FCSTD DOCUMENT  (FreeCAD 1.0R38641 +468 (Git))
Label: cad_assembly
License: All rights reserved
LicenseURL: https://en.wikipedia.org/wiki/All_rights_reserved
objects: App::Link×18, App::FeaturePython×17, Assembly::JointGroup×1, Assembly::AssemblyObject×1
EXTERNAL_REF file=cad_frame_top.FCStd obj=Body
EXTERNAL_REF file=k1_motor_mount_left.FCStd obj=Part
EXTERNAL_REF file=k1_motor_mount_right.FCStd obj=Part
EXTERNAL_REF file=k1_front_idler_left.FCStd obj=Part
EXTERNAL_REF file=k1_front_idler_right.FCStd obj=Part
EXTERNAL_REF file=k1_joint_left.FCStd obj=Part
EXTERNAL_REF file=cad_rail_mgn12_x.FCStd obj=Body
EXTERNAL_REF file=k1_joint_right.FCStd obj=Part
EXTERNAL_REF file=k1_rail_mount.FCStd obj=Part
EXTERNAL_REF file=k1_tensioner_left.FCStd obj=Part
EXTERNAL_REF file=k1_tensioner_right.FCStd obj=Part
EXTERNAL_REF file=cad_20x10x2.FCStd obj=Body
EXTERNAL_REF file=k1_toolhead_20x10.FCStd obj=Part
EXTERNAL_REF file=cad_rail_mgn12_y.FCStd obj=Body
EXTERNAL_REF file=k1_motor_mount_couplers_stock_left.FCStd obj=Part
EXTERNAL_REF file=k1_motor_mount_couplers_stock_right.FCStd obj=Part

FEATURE [App::Link] cad_frame_top
  LinkPlacement = pos=(0,0,0) rot=(-0.926776,-0.056516,-0.371338;0rad)
  LinkedObject = -> <external cad_frame_top.FCStd>#Body
  Placement = pos=(0,0,0) rot=(-0.926776,-0.056516,-0.371338;0rad)
FEATURE [App::FeaturePython] GroundedJoint  # Assembly grounded joint (typed FeaturePython)
  ObjectToGround = -> cad_frame_top
  Placement = pos=(0,0,0) rot=(-0.927137,-0.056538,-0.371482;0rad)
FEATURE [App::Link] k1_motor_mount_left_part
  LinkPlacement = pos=(-212.641,150.472,-35.0551) rot=(-0.926776,-0.056516,-0.371338;0rad)
  LinkedObject = -> <external k1_motor_mount_left.FCStd>#Part
  Placement = pos=(-212.641,150.472,-35.0551) rot=(-0.926776,-0.056516,-0.371338;0rad)
FEATURE [App::FeaturePython] Joint  label="frame_motor_left"  # Assembly joint (typed FeaturePython)
  Activated = true
  AngleMax = 0
  AngleMin = 0
  Detach1 = false
  Detach2 = false
  Distance = 0
  Distance2 = 0
  EnableAngleMax = false
  EnableAngleMin = false
  EnableLengthMax = false
  EnableLengthMin = false
  JointType = 0 (Fixed)
  LengthMax = 0
  LengthMin = 0
  Offset2 = pos=(0,0,0) rot=(0,0,1;1.5708rad)
  Placement1 = pos=(52.6406,991.528,40.055) rot=(-0.707107,0,0.707107;3.14159rad)
  Placement2 = pos=(-212,192,5) rot=(0,-1.00039,0;4.71239rad)
  Reference1 = -> Assembly [k1_motor_mount_left_part.Body.Edge272,k1_motor_mount_left_part.Body.Edge272]
  Reference2 = -> Assembly [cad_frame_top.Edge152,cad_frame_top.Edge152]
FEATURE [App::Link] k1_motor_mount_right_part
  LinkPlacement = pos=(135.359,150.472,-35.055) rot=(-0.926776,-0.056516,-0.371338;0rad)
  LinkedObject = -> <external k1_motor_mount_right.FCStd>#Part
  Placement = pos=(135.359,150.472,-35.055) rot=(-0.926776,-0.056516,-0.371338;0rad)
FEATURE [App::FeaturePython] Joint001  label="frame_motor_right"  # Assembly joint (typed FeaturePython)
  Activated = true
  AngleMax = 0
  AngleMin = 0
  Detach1 = false
  Detach2 = false
  Distance = 0
  Distance2 = 0
  EnableAngleMax = false
  EnableAngleMin = false
  EnableLengthMax = false
  EnableLengthMin = false
  JointType = 0 (Fixed)
  LengthMax = 0
  LengthMin = 0
  Offset2 = pos=(0,0,0) rot=(0,0,-1;1.5708rad)
  Placement1 = pos=(305.641,991.528,40.055) rot=(0,-1,0;1.5708rad)
  Placement2 = pos=(212,192,5) rot=(0.707382,0,0.707382;3.14159rad)
  Reference1 = -> Assembly [k1_motor_mount_right_part.Body.Edge6,k1_motor_mount_right_part.Body.Edge6]
  Reference2 = -> Assembly [cad_frame_top.Edge216,cad_frame_top.Edge216]
FEATURE [App::Link] k1_front_idler_left_part
  LinkPlacement = pos=(-212,-211.265,-35.0549) rot=(-0.926776,-0.056516,-0.371338;0rad)
  LinkedObject = -> <external k1_front_idler_left.FCStd>#Part
  Placement = pos=(-212,-211.265,-35.0549) rot=(-0.926776,-0.056516,-0.371338;0rad)
FEATURE [App::Link] k1_front_idler_right_part
  LinkPlacement = pos=(212,-211.265,-35.0549) rot=(-0.926776,-0.056516,-0.371338;0rad)
  LinkedObject = -> <external k1_front_idler_right.FCStd>#Part
  Placement = pos=(212,-211.265,-35.0549) rot=(-0.926776,-0.056516,-0.371338;0rad)
FEATURE [App::Link] k1_joint_left_part
  LinkPlacement = pos=(-182.615,35.6211,-29.1099) rot=(0.57735,-0.57735,0.57735;2.0944rad)
  LinkedObject = -> <external k1_joint_left.FCStd>#Part
  Placement = pos=(-182.615,35.6211,-29.1099) rot=(0.57735,-0.57735,0.57735;2.0944rad)
FEATURE [App::FeaturePython] Joint007  label="frame_front_idler_right"  # Assembly joint (typed FeaturePython)
  Activated = true
  AngleMax = 0
  AngleMin = 0
  Detach1 = false
  Detach2 = false
  Distance = 0
  Distance2 = 0
  EnableAngleMax = false
  EnableAngleMin = false
  EnableLengthMax = false
  EnableLengthMin = false
  JointType = 0 (Fixed)
  LengthMax = 0
  LengthMin = 0
  Placement1 = pos=(212,-192,5) rot=(0.577575,0.577575,0.577575;2.0944rad)
  Placement2 = pos=(0,19.265,40.055) rot=(0.57735,0.57735,0.57735;2.0944rad)
  Reference1 = -> Assembly [cad_frame_top.Edge217,cad_frame_top.Edge217]
  Reference2 = -> Assembly [k1_front_idler_right_part.Body.Edge47,k1_front_idler_right_part.Body.Edge47]
FEATURE [App::Link] cad_rail_mgn12_x
  LinkPlacement = pos=(191.885,27.491,-25.2799) rot=(0.57735,0.57735,-0.57735;4.18879rad)
  LinkedObject = -> <external cad_rail_mgn12_x.FCStd>#Body
  Placement = pos=(191.885,27.491,-25.2799) rot=(0.57735,0.57735,-0.57735;4.18879rad)
FEATURE [App::Link] k1_joint_right_part
  LinkPlacement = pos=(182.385,35.621,-29.1099) rot=(0.57735,-0.57735,0.57735;2.0944rad)
  LinkedObject = -> <external k1_joint_right.FCStd>#Part
  Placement = pos=(182.385,35.621,-29.1099) rot=(0.57735,-0.57735,0.57735;2.0944rad)
FEATURE [App::FeaturePython] Joint011  label="frame_front_idler_left"  # Assembly joint (typed FeaturePython)
  Activated = true
  AngleMax = 0
  AngleMin = 0
  Detach1 = false
  Detach2 = false
  Distance = 0
  Distance2 = 0
  EnableAngleMax = false
  EnableAngleMin = false
  EnableLengthMax = false
  EnableLengthMin = false
  JointType = 0 (Fixed)
  LengthMax = 0
  LengthMin = 0
  Offset2 = pos=(0,0,0) rot=(0,0,1;3.14159rad)
  Placement1 = pos=(-212,-192,5) rot=(0.577575,0.577575,0.577575;2.0944rad)
  Placement2 = pos=(0,19.265,40.055) rot=(0.57735,0.57735,-0.57735;4.18879rad)
  Reference1 = -> Assembly [cad_frame_top.Edge153,cad_frame_top.Edge153]
  Reference2 = -> Assembly [k1_front_idler_left_part.Body.Edge12,k1_front_idler_left_part.Body.Edge12]
FEATURE [App::Link] k1_rail_mount_part  label="k1_rail_mount_left"
  LinkPlacement = pos=(187.115,-20.5,12.89) rot=(-0.926775,-0.056516,-0.371338;0rad)
  LinkedObject = -> <external k1_rail_mount.FCStd>#Part
  Placement = pos=(187.115,-20.5,12.89) rot=(-0.926775,-0.056516,-0.371338;0rad)
FEATURE [App::Link] k1_rail_mount_part001  label="k1_rail_mount_right"
  LinkPlacement = pos=(-187.115,19.5,12.89) rot=(0,0,1;3.14159rad)
  LinkedObject = -> <external k1_rail_mount.FCStd>#Part
  Placement = pos=(-187.115,19.5,12.89) rot=(0,0,1;3.14159rad)
FEATURE [App::Link] k1_tensioner_left_part
  LinkPlacement = pos=(-174.295,195.1,4.54494) rot=(0.57735,0.57735,0.57735;2.0944rad)
  LinkedObject = -> <external k1_tensioner_left.FCStd>#Part
  Placement = pos=(-174.295,195.1,4.54494) rot=(0.57735,0.57735,0.57735;2.0944rad)
FEATURE [App::FeaturePython] Joint014  label="motor_left_tensioner"  # Assembly joint (typed FeaturePython)
  Activated = true
  AngleMax = 0
  AngleMin = 0
  Detach1 = false
  Detach2 = false
  Distance = 0
  Distance2 = 0
  EnableAngleMax = false
  EnableAngleMin = false
  EnableLengthMax = false
  EnableLengthMin = false
  JointType = 3 (Slider)
  LengthMax = 0
  LengthMin = 0
  Offset2 = pos=(0,0,0) rot=(0,0,1;1.5708rad)
  Placement1 = pos=(7,-27.15,2) rot=(0,0,1;0rad)
  Placement2 = pos=(86.3406,1001.63,12.45) rot=(-0.57735,-0.57735,0.57735;2.0944rad)
  Reference1 = -> Assembly [k1_tensioner_left_part.Body.Edge23,k1_tensioner_left_part.Body.Edge23]
  Reference2 = -> Assembly [k1_motor_mount_left_part.Body.Edge192,k1_motor_mount_left_part.Body.Edge192]
FEATURE [App::Link] k1_tensioner_right_part
  LinkPlacement = pos=(175.227,205.85,2.49494) rot=(-0.57735,0.57735,0.57735;4.18879rad)
  LinkedObject = -> <external k1_tensioner_right.FCStd>#Part
  Placement = pos=(175.227,205.85,2.49494) rot=(-0.57735,0.57735,0.57735;4.18879rad)
FEATURE [App::FeaturePython] Joint015  label="motor_right_tensioner"  # Assembly joint (typed FeaturePython)
  Activated = true
  AngleMax = 0
  AngleMin = 0
  Detach1 = false
  Detach2 = false
  Distance = 0
  Distance2 = 0
  EnableAngleMax = false
  EnableAngleMin = false
  EnableLengthMax = false
  EnableLengthMin = false
  JointType = 3 (Slider)
  LengthMax = 0
  LengthMin = 0
  Offset2 = pos=(0,0,0) rot=(0,0,1;1.5708rad)
  Placement1 = pos=(3.75,-9,2) rot=(0,0,1;0rad)
  Placement2 = pos=(271.941,1001.63,28.55) rot=(-0.57735,0.57735,0.57735;4.18879rad)
  Reference1 = -> Assembly [k1_tensioner_right_part.Body.Edge78,k1_tensioner_right_part.Body.Edge78]
  Reference2 = -> Assembly [k1_motor_mount_right_part.Body.Edge283,k1_motor_mount_right_part.Body.Edge283]
FEATURE [App::Link] cad_20x10x2
  LinkPlacement = pos=(204.385,31.491,-34.2799) rot=(0.707107,0.707107,0;3.14159rad)
  LinkedObject = -> <external cad_20x10x2.FCStd>#Body
  Placement = pos=(204.385,31.491,-34.2799) rot=(0.707107,0.707107,0;3.14159rad)
FEATURE [App::Link] k1_toolhead_20x10_part
  LinkPlacement = pos=(-33.1127,27.001,-47.3799) rot=(0,0,1;4.71239rad)
  LinkedObject = -> <external k1_toolhead_20x10.FCStd>#Part
  Placement = pos=(-33.1127,27.001,-47.3799) rot=(0,0,1;4.71239rad)
FEATURE [App::Link] cad_rail_mgn12_y
  LinkPlacement = pos=(-192.115,192,9.88994) rot=(0,-0.707107,0.707107;3.14159rad)
  LinkedObject = -> <external cad_rail_mgn12_y.FCStd>#Body
  Placement = pos=(-192.115,192,9.88994) rot=(0,-0.707107,0.707107;3.14159rad)
FEATURE [App::FeaturePython] Joint018  label="motor_mount_left_rail"  # Assembly joint (typed FeaturePython)
  Activated = true
  AngleMax = 0
  AngleMin = 0
  Detach1 = false
  Detach2 = false
  Distance = 0
  Distance2 = 0
  EnableAngleMax = false
  EnableAngleMin = false
  EnableLengthMax = false
  EnableLengthMin = false
  JointType = 0 (Fixed)
  LengthMax = 0
  LengthMin = 0
  Offset2 = pos=(0,0,0) rot=(0,0,1;3.14159rad)
  Placement1 = pos=(-2.84e-14,4,5) rot=(1,0,0;1.5708rad)
  Placement2 = pos=(72.5256,986.528,40.945) rot=(0,0,1;3.14159rad)
  Reference1 = -> Assembly [cad_rail_mgn12_y.Edge20,cad_rail_mgn12_y.Edge20]
  Reference2 = -> Assembly [k1_motor_mount_left_part.Body.Edge252,k1_motor_mount_left_part.Body.Edge252]
FEATURE [App::Link] cad_rail_mgn12_y001
  LinkPlacement = pos=(192.115,192,9.88994) rot=(1,0,0;1.5708rad)
  LinkedObject = -> <external cad_rail_mgn12_y.FCStd>#Body
  Placement = pos=(192.115,192,9.88994) rot=(1,0,0;1.5708rad)
FEATURE [App::FeaturePython] Joint019  label="motor_mount_right_rail"  # Assembly joint (typed FeaturePython)
  Activated = true
  AngleMax = 0
  AngleMin = 0
  Detach1 = false
  Detach2 = false
  Distance = 0
  Distance2 = 0
  EnableAngleMax = false
  EnableAngleMin = false
  EnableLengthMax = false
  EnableLengthMin = false
  JointType = 0 (Fixed)
  LengthMax = 0
  LengthMin = 0
  Placement1 = pos=(-8.53e-14,-4,5) rot=(1,0,0;1.5708rad)
  Placement2 = pos=(285.756,986.528,40.945) rot=(0,0,1;0rad)
  Reference1 = -> Assembly [cad_rail_mgn12_y001.Edge59,cad_rail_mgn12_y001.Edge59]
  Reference2 = -> Assembly [k1_motor_mount_right_part.Body.Edge206,k1_motor_mount_right_part.Body.Edge206]
FEATURE [App::FeaturePython] Joint020  label="rail_left_joint"  # Assembly joint (typed FeaturePython)
  Activated = true
  AngleMax = 0
  AngleMin = 0
  Detach1 = false
  Detach2 = false
  Distance = 0
  Distance2 = 0
  EnableAngleMax = false
  EnableAngleMin = false
  EnableLengthMax = false
  EnableLengthMin = false
  JointType = 3 (Slider)
  LengthMax = 0
  LengthMin = 0
  Offset2 = pos=(0,0,0) rot=(0,0,-1;1.5708rad)
  Placement1 = pos=(22.7,6,5) rot=(0.707107,0,0.707107;3.14159rad)
  Placement2 = pos=(6,4,192.5) rot=(0,0,-1;1.5708rad)
  Reference1 = -> Assembly [k1_joint_left_part.Link.Edge36,k1_joint_left_part.Link.Edge36]
  Reference2 = -> Assembly [cad_rail_mgn12_y.Edge4,cad_rail_mgn12_y.Edge4]
FEATURE [App::FeaturePython] Joint021  label="joint_left_rail_x"  # Assembly joint (typed FeaturePython)
  Activated = true
  AngleMax = 0
  AngleMin = 0
  Detach1 = false
  Detach2 = false
  Distance = 0
  Distance2 = 0
  EnableAngleMax = false
  EnableAngleMin = false
  EnableLengthMax = false
  EnableLengthMin = false
  JointType = 0 (Fixed)
  LengthMax = 0
  LengthMin = 0
  Offset2 = pos=(0,0,0) rot=(0,0,-1;1.5708rad)
  Placement1 = pos=(3.6e-15,-4,380) rot=(-1,0,0;4.71239rad)
  Placement2 = pos=(7.83,5.5,8.13) rot=(0,1,0;1.5708rad)
  Reference1 = -> Assembly [cad_rail_mgn12_x.Edge29,cad_rail_mgn12_x.Edge29]
  Reference2 = -> Assembly [k1_joint_left_part.Body.Edge81,k1_joint_left_part.Body.Edge81]
FEATURE [App::FeaturePython] Joint022  label="rail_x_toolhead"  # Assembly joint (typed FeaturePython)
  Activated = true
  AngleMax = 0
  AngleMin = 0
  Detach1 = false
  Detach2 = false
  Distance = 0
  Distance2 = 0
  EnableAngleMax = false
  EnableAngleMin = false
  EnableLengthMax = false
  EnableLengthMin = false
  JointType = 3 (Slider)
  LengthMax = 0
  LengthMin = 0
  Offset2 = pos=(0,0,0) rot=(0,0,1;1.5708rad)
  Placement1 = pos=(22.7,-6,5) rot=(0.707107,0,0.707107;3.14159rad)
  Placement2 = pos=(6,-4,192.5) rot=(0,0,1;1.5708rad)
  Reference1 = -> Assembly [k1_toolhead_20x10_part.Link.Edge35,k1_toolhead_20x10_part.Link.Edge35]
  Reference2 = -> Assembly [cad_rail_mgn12_x.Edge59,cad_rail_mgn12_x.Edge59]
FEATURE [App::FeaturePython] Joint023  label="rail_x_20x10"  # Assembly joint (typed FeaturePython)
  Activated = true
  AngleMax = 0
  AngleMin = 0
  Detach1 = false
  Detach2 = false
  Distance = 0
  Distance2 = 0
  EnableAngleMax = false
  EnableAngleMin = false
  EnableLengthMax = false
  EnableLengthMin = false
  JointType = 0 (Fixed)
  LengthMax = 0
  LengthMin = 0
  Offset2 = pos=(0,0,0) rot=(0,0,1;3.14159rad)
  Placement1 = pos=(-4,-392.5,-5) rot=(0,0,-1;3.14159rad)
  Placement2 = pos=(3.6e-15,4,380) rot=(0,0.707107,-0.707107;3.14159rad)
  Reference1 = -> Assembly [cad_20x10x2.Edge13,cad_20x10x2.Edge13]
  Reference2 = -> Assembly [cad_rail_mgn12_x.Edge9,cad_rail_mgn12_x.Edge9]
FEATURE [App::FeaturePython] Joint024  label="rail_x_joint_right"  # Assembly joint (typed FeaturePython)
  Activated = true
  AngleMax = 0
  AngleMin = 0
  Detach1 = false
  Detach2 = false
  Distance = 0
  Distance2 = 0
  EnableAngleMax = false
  EnableAngleMin = false
  EnableLengthMax = false
  EnableLengthMin = false
  JointType = 0 (Fixed)
  LengthMax = 0
  LengthMin = 0
  Offset1 = pos=(-1,0,0) rot=(0,0,1;0rad)
  Offset2 = pos=(0,0,0) rot=(0,0,-1;1.5708rad)
  Placement1 = pos=(7.83,-4.5,8.13) rot=(-0.57735,0.57735,0.57735;4.18879rad)
  Placement2 = pos=(-4.26e-14,-4,5) rot=(-0.57735,-0.57735,0.57735;4.18879rad)
  Reference1 = -> Assembly [k1_joint_right_part.Body.Edge80,k1_joint_right_part.Body.Edge80]
  Reference2 = -> Assembly [cad_rail_mgn12_x.Edge43,cad_rail_mgn12_x.Edge43]
FEATURE [App::FeaturePython] Joint025  label="rail_right_mount"  # Assembly joint (typed FeaturePython)
  Activated = true
  AngleMax = 0
  AngleMin = 0
  Detach1 = false
  Detach2 = false
  Distance = 0
  Distance2 = 0
  EnableAngleMax = false
  EnableAngleMin = false
  EnableLengthMax = false
  EnableLengthMin = false
  JointType = 0 (Fixed)
  LengthMax = 0
  LengthMin = 0
  Placement1 = pos=(5,32.5,1) rot=(1,0,0;3.14159rad)
  Placement2 = pos=(-2.84e-14,4,180) rot=(1,0,0;1.5708rad)
  Reference1 = -> Assembly [k1_rail_mount_part.Body.Edge3,k1_rail_mount_part.Body.Edge3]
  Reference2 = -> Assembly [cad_rail_mgn12_y001.Edge13,cad_rail_mgn12_y001.Edge13]
FEATURE [App::FeaturePython] Joint026  label="rail_left_mount"  # Assembly joint (typed FeaturePython)
  Activated = true
  AngleMax = 0
  AngleMin = 0
  Detach1 = false
  Detach2 = false
  Distance = 0
  Distance2 = 0
  EnableAngleMax = false
  EnableAngleMin = false
  EnableLengthMax = false
  EnableLengthMin = false
  JointType = 0 (Fixed)
  LengthMax = 0
  LengthMin = 0
  Placement1 = pos=(-2.84e-14,-4,180) rot=(1,0,0;1.5708rad)
  Placement2 = pos=(5,7.5,1) rot=(1,0,0;3.14159rad)
  Reference1 = -> Assembly [cad_rail_mgn12_y.Edge45,cad_rail_mgn12_y.Edge45]
  Reference2 = -> Assembly [k1_rail_mount_part001.Body.Edge8,k1_rail_mount_part001.Body.Edge8]
FEATURE [App::Link] k1_motor_mount_couplers_stock_left_part
  LinkPlacement = pos=(-214.641,100.472,-35.055) rot=(0,0,1;0rad)
  LinkedObject = -> <external k1_motor_mount_couplers_stock_left.FCStd>#Part
  Placement = pos=(-214.641,100.472,-35.055) rot=(0,0,1;0rad)
FEATURE [App::Link] k1_motor_mount_couplers_stock_right_part
  LinkPlacement = pos=(106.359,100.472,-103.055) rot=(-0.926776,-0.056515,-0.371338;0rad)
  LinkedObject = -> <external k1_motor_mount_couplers_stock_right.FCStd>#Part
  Placement = pos=(106.359,100.472,-103.055) rot=(-0.926776,-0.056515,-0.371338;0rad)
FEATURE [App::FeaturePython] Joint027  label="rail_right_mount001"  # Assembly joint (typed FeaturePython)
  Activated = true
  AngleMax = 0
  AngleMin = 0
  Detach1 = false
  Detach2 = false
  Distance = 0
  Distance2 = 0
  EnableAngleMax = false
  EnableAngleMin = false
  EnableLengthMax = false
  EnableLengthMin = false
  JointType = 0 (Fixed)
  LengthMax = 0
  LengthMin = 0
  Offset2 = pos=(0,0,0) rot=(0,0,1;3.14159rad)
  Placement1 = pos=(305.641,991.528,40.055) rot=(0.57735,0.57735,0.57735;2.0944rad)
  Placement2 = pos=(212,192,5) rot=(-0.577575,-0.577575,-0.577575;4.18879rad)
  Reference1 = -> Assembly [k1_motor_mount_couplers_stock_right_part.Body.Edge153,k1_motor_mount_couplers_stock_right_part.Body.Edge153]
  Reference2 = -> Assembly [cad_frame_top.Edge216,cad_frame_top.Edge216]
FEATURE [Assembly::JointGroup] Joints
  Group = -> [GroundedJoint,Joint,Joint001,Joint007,Joint011,Joint014,Joint015,Joint018,Joint019,Joint020,Joint021,Joint022,Joint023,Joint024,Joint025,Joint026,Joint027]
FEATURE [Assembly::AssemblyObject] Assembly
  Group = -> [Joints,cad_frame_top,GroundedJoint,k1_motor_mount_left_part,Joint,k1_motor_mount_right_part,Joint001,k1_front_idler_left_part,k1_front_idler_right_part,k1_joint_left_part,Joint007,cad_rail_mgn12_x,k1_joint_right_part,Joint011,k1_rail_mount_part,k1_rail_mount_part001,k1_tensioner_left_part,Joint014,k1_tensioner_right_part,Joint015,cad_20x10x2,k1_toolhead_20x10_part,cad_rail_mgn12_y,Joint018,+12 more]
  Origin = -> Origin
  Type = Assembly

RESOLVED EXTERNAL PARTS (link-assembly join: the EXTERNAL_REF files above that resolve inside this repo's crawl, each included once):
---- part cad_20x10x2.FCStd = doc fcstd_428c16497015 ----
FCSTD DOCUMENT  (FreeCAD 1.0R38641 +468 (Git))
Label: cad_20x10x2
License: All rights reserved
LicenseURL: https://en.wikipedia.org/wiki/All_rights_reserved
objects: Sketcher::SketchObject×2, PartDesign::Pad×1, PartDesign::Pocket×1, PartDesign::Body×1
note: 11 computed .brp shape members not serialized (recipe doc carries the construction recipe); baked Part::Feature solids carry a one-line shape summary decoded from their .brp

FEATURE [Sketcher::SketchObject] Sketch
  ArcFitTolerance = 1e-06
  AttachmentSupport = -> [XZ_Plane]
  FullyConstrained = true
  MakeInternals = false
  MapMode = 5
  Placement = pos=(0,0,0) rot=(1,0,0;1.5708rad)
  sketch-geometry (8):
    g0: LineSegment StartX=-8 StartY=3 StartZ=0 EndX=-8 EndY=-3 EndZ=0
    g1: LineSegment StartX=-8 StartY=-3 StartZ=0 EndX=8 EndY=-3 EndZ=0
    g2: LineSegment StartX=8 StartY=-3 StartZ=0 EndX=8 EndY=3 EndZ=0
    g3: LineSegment StartX=8 StartY=3 StartZ=0 EndX=-8 EndY=3 EndZ=0
    g4: LineSegment StartX=-10 StartY=5 StartZ=0 EndX=-10 EndY=-5 EndZ=0
    g5: LineSegment StartX=-10 StartY=-5 StartZ=0 EndX=10 EndY=-5 EndZ=0
    g6: LineSegment StartX=10 StartY=-5 StartZ=0 EndX=10 EndY=5 EndZ=0
    g7: LineSegment StartX=10 StartY=5 StartZ=0 EndX=-10 EndY=5 EndZ=0
  constraints (20):
    c: Coincident(g0,g1)
    c: Coincident(g1,g2)
    c: Coincident(g2,g3)
    c: Coincident(g3,g0)
    c: Vertical(g2)
    c: Horizontal(g1)
    c: Coincident(g4,g5)
    c: Coincident(g5,g6)
    c: Coincident(g6,g7)
    c: Coincident(g7,g4)
    c: Vertical(g6)
    c: Horizontal(g5)
    c: Distance(g7,g7) = 20
    c: DistanceY(g6,g6) = 10
    c: Distance(g3,g3) = 16
    c: Distance(g0,g0) = 6
    c: Symmetric(g4,g6,g-2)
    c: Symmetric(g4,g4,g-1)
    c: Symmetric(g0,g2,g-2)
    c: Symmetric(g0,g0,g-1)
FEATURE [PartDesign::Pad] Pad
  Direction = (0,-1,2e-16)
  Length = 410
  Length2 = 10
  Placement = pos=(0,0,0) rot=(1,0,0;1.5708rad)
  Profile = -> Sketch
  ReferenceAxis = -> Sketch [N_Axis]
  Refine = true
  Suppressed = false
  Type = 0
FEATURE [Sketcher::SketchObject] Sketch001
  ArcFitTolerance = 1e-06
  AttachmentSupport = -> [Pad]
  ExternalGeometry = -> [Pad]
  FullyConstrained = true
  MakeInternals = false
  MapMode = 5
  Placement = pos=(0,1.1e-15,5) rot=(0,0,1;3.14159rad)
  sketch-geometry (3):
    g0: LineSegment [constr] StartX=4 StartY=410 StartZ=0 EndX=4 EndY=0 EndZ=0
    g1: Circle CenterX=4 CenterY=17.5 CenterZ=0 NormalX=0 NormalY=0 NormalZ=1 AngleXU=0 Radius=1.5
    g2: Circle CenterX=4 CenterY=392.5 CenterZ=0 NormalX=0 NormalY=0 NormalZ=1 AngleXU=0 Radius=1.5
  constraints (10):
    c: PointOnObject(g0,g-3)
    c: PointOnObject(g0,g-1)
    c: Vertical(g0)
    c: PointOnObject(g1,g0)
    c: PointOnObject(g2,g0)
    c: Equal(g2,g1)
    c: Diameter(g1) = 3
    c: Distance(g1,g-1) = 17.5
    c: Distance(g2,g-3) = 17.5
    c: Distance(g0,g-4) = 6
FEATURE [PartDesign::Pocket] Pocket
  BaseFeature = -> Pad
  Direction = (0,0,-1)
  Length = 5
  Length2 = 5
  Placement = pos=(0,0,0) rot=(1,0,0;1.5708rad)
  Profile = -> Sketch001
  ReferenceAxis = -> Sketch001 [N_Axis]
  Refine = true
  Suppressed = false
  Type = 1
FEATURE [PartDesign::Body] Body  label="cad_20x10x2"
  AllowCompound = false
  Group = -> [Sketch,Pad,Sketch001,Pocket]
  Origin = -> Origin
  Tip = -> Pocket
---- part cad_frame_top.FCStd = doc fcstd_c45ce3313788 ----
FCSTD DOCUMENT  (FreeCAD 1.0R38641 +468 (Git))
Label: cad_frame_top
License: All rights reserved
LicenseURL: https://en.wikipedia.org/wiki/All_rights_reserved
objects: Part::Feature×1, PartDesign::FeatureBase×1, PartDesign::Body×1
note: 4 computed .brp shape members not serialized (recipe doc carries the construction recipe); baked Part::Feature solids carry a one-line shape summary decoded from their .brp

FEATURE [Part::Feature] Part__Feature  label="step"
  shape: bbox 438.3 x 438.3 x 56.64 mm, 119 faces (baked)
FEATURE [PartDesign::FeatureBase] BaseFeature
  BaseFeature = -> Part__Feature
  Suppressed = false
FEATURE [PartDesign::Body] Body  label="cad_frame_top"
  AllowCompound = false
  BaseFeature = -> Part__Feature
  Group = -> [BaseFeature]
  Origin = -> Origin
  Tip = -> BaseFeature
---- part cad_rail_mgn12_x.FCStd = doc fcstd_ab6c7a5a6af0 ----
FCSTD DOCUMENT  (FreeCAD 1.0R38641 +468 (Git))
Label: cad_rail_mgn12_x
License: All rights reserved
LicenseURL: https://en.wikipedia.org/wiki/All_rights_reserved
objects: PartDesign::Pad×3, Sketcher::SketchObject×2, PartDesign::Pocket×1, PartDesign::LinearPattern×1, PartDesign::Body×1
note: 19 computed .brp shape members not serialized (recipe doc carries the construction recipe); baked Part::Feature solids carry a one-line shape summary decoded from their .brp

FEATURE [Sketcher::SketchObject] Sketch
  ArcFitTolerance = 0
  AttachmentSupport = -> [XY_Plane]
  FullyConstrained = true
  MakeInternals = false
  MapMode = 5
  sketch-geometry (4):
    g0: LineSegment StartX=-6 StartY=4 StartZ=0 EndX=6 EndY=4 EndZ=0
    g1: LineSegment StartX=6 StartY=4 StartZ=0 EndX=6 EndY=-4 EndZ=0
    g2: LineSegment StartX=6 StartY=-4 StartZ=0 EndX=-6 EndY=-4 EndZ=0
    g3: LineSegment StartX=-6 StartY=-4 StartZ=0 EndX=-6 EndY=4 EndZ=0
  constraints (10):
    c: Coincident(g0,g1)
    c: Coincident(g1,g2)
    c: Coincident(g2,g3)
    c: Coincident(g3,g0)
    c: Horizontal(g2)
    c: Vertical(g1)
    c: Symmetric(g0,g0,g-2)
    c: Symmetric(g0,g2,g-1)
    c: Distance(g0) = 12
    c: Distance(g3) = 8
FEATURE [PartDesign::Pad] Pad
  Direction = (0,0,1)
  Length = 385
  Length2 = 10
  Profile = -> Sketch
  ReferenceAxis = -> Sketch [N_Axis]
  Suppressed = false
  Type = 0
FEATURE [Sketcher::SketchObject] Sketch001
  ArcFitTolerance = 0
  AttachmentSupport = -> [Pad]
  ExternalGeometry = -> [Pad]
  FullyConstrained = true
  MakeInternals = false
  MapMode = 5
  Placement = pos=(0,-4,0) rot=(1,0,0;1.5708rad)
  sketch-geometry (1):
    g0: Circle CenterX=0 CenterY=380 CenterZ=0 NormalX=0 NormalY=0 NormalZ=1 AngleXU=0 Radius=1.5
  constraints (3):
    c: PointOnObject(g0,g-2)
    c: Radius(g0) = 1.5
    c: Distance(g0,g-3) = 5
FEATURE [PartDesign::Pocket] Pocket
  BaseFeature = -> Pad
  Direction = (0,1,-2e-16)
  Length = 5
  Length2 = 5
  Profile = -> Sketch001
  ReferenceAxis = -> Sketch001 [N_Axis]
  Suppressed = false
  Type = 1
FEATURE [PartDesign::LinearPattern] LinearPattern
  BaseFeature = -> Pocket
  Direction = -> Z_Axis
  Length = 375
  Mode = 0
  Occurrences = 16
  Offset = 25
  Originals = -> [Pocket]
  Reversed = true
  Suppressed = false
  TransformMode = 0
FEATURE [PartDesign::Pad] Pad001
  BaseFeature = -> LinearPattern
  Direction = (0,0,-1)
  Length = 12.5
  Length2 = 10
  Profile = -> LinearPattern [Face3]
  Refine = true
  Suppressed = false
  Type = 0
FEATURE [PartDesign::Pad] Pad002
  BaseFeature = -> Pad001
  Direction = (0,0,1)
  Length = 12.5
  Length2 = 10
  Profile = -> Pad001 [Face1]
  Refine = true
  Suppressed = false
  Type = 0
FEATURE [PartDesign::Body] Body  label="cad_rail_mgn12_x"
  AllowCompound = false
  Group = -> [Sketch,Pad,Sketch001,Pocket,LinearPattern,Pad001,Pad002]
  Origin = -> Origin
  Placement = pos=(0,6,4) rot=(0.57735,0.57735,0.57735;2.0944rad)
  Tip = -> Pad002
---- part cad_rail_mgn12_y.FCStd = doc fcstd_a98204ac455e ----
FCSTD DOCUMENT  (FreeCAD 1.0R38641 +468 (Git))
Label: cad_rail_mgn12_y
License: All rights reserved
LicenseURL: https://en.wikipedia.org/wiki/All_rights_reserved
objects: Sketcher::SketchObject×2, PartDesign::Pad×1, PartDesign::Pocket×1, PartDesign::LinearPattern×1, PartDesign::Body×1
note: 13 computed .brp shape members not serialized (recipe doc carries the construction recipe); baked Part::Feature solids carry a one-line shape summary decoded from their .brp

FEATURE [Sketcher::SketchObject] Sketch
  ArcFitTolerance = 0
  AttachmentSupport = -> [XY_Plane]
  FullyConstrained = true
  MakeInternals = false
  MapMode = 5
  sketch-geometry (4):
    g0: LineSegment StartX=-6 StartY=4 StartZ=0 EndX=6 EndY=4 EndZ=0
    g1: LineSegment StartX=6 StartY=4 StartZ=0 EndX=6 EndY=-4 EndZ=0
    g2: LineSegment StartX=6 StartY=-4 StartZ=0 EndX=-6 EndY=-4 EndZ=0
    g3: LineSegment StartX=-6 StartY=-4 StartZ=0 EndX=-6 EndY=4 EndZ=0
  constraints (10):
    c: Coincident(g0,g1)
    c: Coincident(g1,g2)
    c: Coincident(g2,g3)
    c: Coincident(g3,g0)
    c: Horizontal(g2)
    c: Vertical(g1)
    c: Symmetric(g0,g0,g-2)
    c: Symmetric(g0,g2,g-1)
    c: Distance(g0) = 12
    c: Distance(g3) = 8
FEATURE [PartDesign::Pad] Pad
  Direction = (0,0,1)
  Length = 385
  Length2 = 10
  Profile = -> Sketch
  ReferenceAxis = -> Sketch [N_Axis]
  Suppressed = false
  Type = 0
FEATURE [Sketcher::SketchObject] Sketch001
  ArcFitTolerance = 0
  AttachmentSupport = -> [Pad]
  ExternalGeometry = -> [Pad]
  FullyConstrained = true
  MakeInternals = false
  MapMode = 5
  Placement = pos=(0,-4,0) rot=(1,0,0;1.5708rad)
  sketch-geometry (1):
    g0: Circle CenterX=0 CenterY=380 CenterZ=0 NormalX=0 NormalY=0 NormalZ=1 AngleXU=0 Radius=1.5
  constraints (3):
    c: PointOnObject(g0,g-2)
    c: Radius(g0) = 1.5
    c: Distance(g0,g-3) = 5
FEATURE [PartDesign::Pocket] Pocket
  BaseFeature = -> Pad
  Direction = (0,1,-2e-16)
  Length = 5
  Length2 = 5
  Profile = -> Sketch001
  ReferenceAxis = -> Sketch001 [N_Axis]
  Suppressed = false
  Type = 1
FEATURE [PartDesign::LinearPattern] LinearPattern
  BaseFeature = -> Pocket
  Direction = -> Z_Axis
  Length = 375
  Mode = 0
  Occurrences = 16
  Offset = 25
  Originals = -> [Pocket]
  Reversed = true
  Suppressed = false
  TransformMode = 0
FEATURE [PartDesign::Body] Body  label="cad_rail_mgn12_y"
  AllowCompound = false
  Group = -> [Sketch,Pad,Sketch001,Pocket,LinearPattern]
  Origin = -> Origin
  Placement = pos=(0,6,4) rot=(0.57735,0.57735,0.57735;2.0944rad)
  Tip = -> LinearPattern
---- part k1_front_idler_left.FCStd = doc fcstd_321a89ae677e ----
FCSTD DOCUMENT  (FreeCAD 1.0R38641 +468 (Git))
Label: k1_front_idler_left
License: All rights reserved
LicenseURL: https://en.wikipedia.org/wiki/All_rights_reserved
objects: Part::Feature×1, PartDesign::FeatureBase×1, PartDesign::Body×1, App::Link×1, App::Part×1
note: 4 computed .brp shape members not serialized (recipe doc carries the construction recipe); baked Part::Feature solids carry a one-line shape summary decoded from their .brp
EXTERNAL_REF file=cad_powge_pulley.FCStd obj=Part

FEATURE [Part::Feature] Part__Feature  label="step"
  shape: bbox 25.99 x 33.8 x 47.95 mm, 39 faces (baked)
FEATURE [PartDesign::FeatureBase] BaseFeature
  BaseFeature = -> Part__Feature
  Suppressed = false
FEATURE [PartDesign::Body] Body  label="k1_front_idler_left"
  AllowCompound = false
  BaseFeature = -> Part__Feature
  Group = -> [BaseFeature]
  Origin = -> Origin001
  Tip = -> BaseFeature
FEATURE [App::Link] Link  label="cad_powge_pulley"
  LinkPlacement = pos=(11.5,17.6,20.825) rot=(0,0,1;0rad)
  LinkedObject = -> <external cad_powge_pulley.FCStd>#Part
  Placement = pos=(11.5,17.6,20.825) rot=(0,0,1;0rad)
FEATURE [App::Part] Part  label="k1_front_idler_left_part"
  Group = -> [Body,Link]
  Origin = -> Origin
---- part k1_front_idler_right.FCStd = doc fcstd_c0961fab244e ----
FCSTD DOCUMENT  (FreeCAD 1.0R38641 +468 (Git))
Label: k1_front_idler_right
License: All rights reserved
LicenseURL: https://en.wikipedia.org/wiki/All_rights_reserved
objects: PartDesign::Pad×2, PartDesign::Pocket×2, Part::Feature×1, PartDesign::FeatureBase×1, App::Link×1, PartDesign::Body×1, App::Part×1
note: 16 computed .brp shape members not serialized (recipe doc carries the construction recipe); baked Part::Feature solids carry a one-line shape summary decoded from their .brp
EXTERNAL_REF file=cad_powge_pulley.FCStd obj=Part

FEATURE [Part::Feature] Part__Feature  label="step"
  shape: bbox 25.99 x 33.8 x 47.95 mm, 40 faces (baked)
FEATURE [PartDesign::FeatureBase] BaseFeature
  BaseFeature = -> Part__Feature
  Suppressed = false
FEATURE [App::Link] Link  label="cad_powge_pulley"
  LinkPlacement = pos=(-11.5,17.6,9.74) rot=(0,0,1;0rad)
  LinkedObject = -> <external cad_powge_pulley.FCStd>#Part
  Placement = pos=(-11.5,17.6,9.74) rot=(0,0,1;0rad)
FEATURE [PartDesign::Pad] Pad
  BaseFeature = -> BaseFeature
  Direction = (0,0,-1)
  Length = 0.7
  Length2 = 10
  Profile = -> BaseFeature [Face35]
  Refine = true
  Suppressed = false
  Type = 0
FEATURE [PartDesign::Pocket] Pocket
  BaseFeature = -> Pad
  Direction = (0,0,-1)
  Length = 0.7
  Length2 = 5
  Profile = -> Pad [Face30]
  Refine = true
  Suppressed = false
  Type = 0
FEATURE [PartDesign::Pad] Pad001
  BaseFeature = -> Pocket
  Direction = (0,0,-1)
  Length = 0.7
  Length2 = 10
  Profile = -> Pocket [Face5]
  Refine = true
  Suppressed = false
  Type = 0
FEATURE [PartDesign::Pocket] Pocket001
  BaseFeature = -> Pad001
  Direction = (0,0,-1)
  Length = 0.7
  Length2 = 5
  Profile = -> Pad001 [Face11]
  Refine = true
  Suppressed = false
  Type = 0
FEATURE [PartDesign::Body] Body  label="k1_front_idler_right"
  AllowCompound = false
  BaseFeature = -> Part__Feature
  Group = -> [BaseFeature,Pad,Pocket,Pad001,Pocket001]
  Origin = -> Origin
  Tip = -> Pocket001
FEATURE [App::Part] Part  label="k1_front_idler_right_part"
  Group = -> [Body,Link]
  Origin = -> Origin001
---- part k1_joint_left.FCStd = doc fcstd_f53bd83b8b9a ----
FCSTD DOCUMENT  (FreeCAD 1.0R38641 +468 (Git))
Label: k1_joint_left
License: All rights reserved
LicenseURL: https://en.wikipedia.org/wiki/All_rights_reserved
objects: PartDesign::Pad×7, Sketcher::SketchObject×7, PartDesign::Pocket×5, App::Link×3, Part::Feature×1, PartDesign::FeatureBase×1, PartDesign::Line×1, PartDesign::Chamfer×1, PartDesign::Body×1, App::Part×1
note: 58 computed .brp shape members not serialized (recipe doc carries the construction recipe); baked Part::Feature solids carry a one-line shape summary decoded from their .brp
EXTERNAL_REF file=cad_mgn12h_block.FCStd obj=Body
EXTERNAL_REF file=cad_powge_pulley.FCStd obj=Part

FEATURE [Part::Feature] Part__Feature  label="step"
  shape: bbox 32.5 x 27 x 53.87 mm, 57 faces (baked)
FEATURE [PartDesign::FeatureBase] BaseFeature
  BaseFeature = -> Part__Feature
  Suppressed = false
FEATURE [PartDesign::Line] DatumLine  label="front_idler_axis"
  AttacherType = Attacher::AttachEngineLine
  AttachmentOffset = pos=(1.495,0,0) rot=(0,0,1;0rad)
  AttachmentSupport = -> [BaseFeature]
  Length = 20
  MapMode = 19
  Placement = pos=(29.9999,4.505,37.83) rot=(0.57735,-0.57735,-0.57735;2.0944rad)
  ResizeMode = 0
FEATURE [PartDesign::Pocket] Pocket
  BaseFeature = -> BaseFeature
  Direction = (1,0,0)
  Length = 0
  Length2 = 5
  Profile = -> BaseFeature [Face32]
  Refine = true
  Suppressed = false
  Type = 3
  UpToFace = -> BaseFeature [Face19]
FEATURE [PartDesign::Pocket] Pocket001
  BaseFeature = -> Pocket
  Direction = (-1,0,0)
  Length = 0
  Length2 = 5
  Profile = -> Pocket [Face48]
  Refine = true
  Suppressed = false
  Type = 3
  UpToFace = -> Pocket [Face17]
FEATURE [PartDesign::Pad] Pad
  BaseFeature = -> Pocket001
  Direction = (1,0,0)
  Length = 10
  Length2 = 10
  Profile = -> Pocket001 [Edge73]
  Refine = true
  Suppressed = false
  Type = 3
  UpToFace = -> Pocket001 [Face22]
FEATURE [PartDesign::Pad] Pad001
  BaseFeature = -> Pad
  Direction = (1,0,0)
  Length = 10
  Length2 = 10
  Profile = -> Pad [Edge42]
  Refine = true
  Suppressed = false
  Type = 3
  UpToFace = -> Pad [Face35]
FEATURE [PartDesign::Pad] Pad002
  BaseFeature = -> Pad001
  Direction = (1,0,0)
  Length = 10
  Length2 = 10
  Profile = -> Pad001 [Edge54]
  Refine = true
  Suppressed = false
  Type = 3
  UpToFace = -> Pad001 [Face10]
FEATURE [Sketcher::SketchObject] Sketch
  ArcFitTolerance = 1e-06
  AttachmentSupport = -> [Pad002]
  ExternalGeometry = -> [DatumLine]
  FullyConstrained = true
  MakeInternals = false
  MapMode = 5
  Placement = pos=(-2.5,0,0) rot=(0.57735,-0.57735,-0.57735;2.0944rad)
  sketch-geometry (1):
    g0: Circle CenterX=-4.505 CenterY=37.83 CenterZ=0 NormalX=0 NormalY=0 NormalZ=1 AngleXU=0 Radius=1.9
  constraints (2):
    c: Coincident(g0,g-3)
    c: Diameter(g0) = 3.8
FEATURE [PartDesign::Pocket] Pocket002
  BaseFeature = -> Pad002
  Direction = (1,0,0)
  Length = 5
  Length2 = 5
  Profile = -> Sketch
  ReferenceAxis = -> Sketch [N_Axis]
  Refine = true
  Suppressed = false
  Type = 1
FEATURE [Sketcher::SketchObject] Sketch001
  ArcFitTolerance = 1e-06
  AttachmentSupport = -> [Pocket002]
  ExternalGeometry = -> [DatumLine]
  FullyConstrained = true
  MakeInternals = false
  MapMode = 5
  Placement = pos=(14.25,0,0) rot=(0.57735,0.57735,0.57735;2.0944rad)
  sketch-geometry (2):
    g0: Circle CenterX=4.505 CenterY=37.83 CenterZ=0 NormalX=0 NormalY=0 NormalZ=1 AngleXU=0 Radius=1.9
    g1: Circle CenterX=4.505 CenterY=37.83 CenterZ=0 NormalX=0 NormalY=0 NormalZ=1 AngleXU=0 Radius=3
  constraints (4):
    c: Coincident(g0,g-3)
    c: Coincident(g1,g0)
    c: Diameter(g0) = 3.8
    c: Diameter(g1) = 6
FEATURE [PartDesign::Pad] Pad003
  BaseFeature = -> Pocket002
  Direction = (1,0,0)
  Length = 0.5
  Length2 = 10
  Profile = -> Sketch001
  ReferenceAxis = -> Sketch001 [N_Axis]
  Refine = true
  Suppressed = false
  Type = 0
FEATURE [Sketcher::SketchObject] Sketch002
  ArcFitTolerance = 1e-06
  AttachmentSupport = -> [Pad003]
  ExternalGeometry = -> [DatumLine]
  FullyConstrained = true
  MakeInternals = false
  MapMode = 5
  Placement = pos=(25.75,0,0) rot=(0.57735,-0.57735,-0.57735;2.0944rad)
  sketch-geometry (2):
    g0: Circle CenterX=-4.505 CenterY=37.83 CenterZ=0 NormalX=0 NormalY=0 NormalZ=1 AngleXU=0 Radius=1.9
    g1: Circle CenterX=-4.505 CenterY=37.83 CenterZ=0 NormalX=0 NormalY=0 NormalZ=1 AngleXU=0 Radius=3
  constraints (4):
    c: Coincident(g0,g-3)
    c: Coincident(g1,g0)
    c: Diameter(g0) = 3.8
    c: Diameter(g1) = 6
FEATURE [PartDesign::Pad] Pad004
  BaseFeature = -> Pad003
  Direction = (-1,0,0)
  Length = 0.5
  Length2 = 10
  Profile = -> Sketch002
  ReferenceAxis = -> Sketch002 [N_Axis]
  Refine = true
  Suppressed = false
  Type = 0
FEATURE [Sketcher::SketchObject] Sketch003
  ArcFitTolerance = 1e-06
  AttachmentSupport = -> [Pad004]
  ExternalGeometry = -> [DatumLine]
  FullyConstrained = true
  MakeInternals = false
  MapMode = 5
  Placement = pos=(-2.5,0,0) rot=(0.57735,-0.57735,-0.57735;2.0944rad)
  sketch-geometry (1):
    g0: Circle CenterX=-4.505 CenterY=37.83 CenterZ=0 NormalX=0 NormalY=0 NormalZ=1 AngleXU=0 Radius=4.5
  constraints (2):
    c: Coincident(g0,g-3)
    c: Diameter(g0) = 9
FEATURE [PartDesign::Pocket] Pocket003
  BaseFeature = -> Pad004
  Direction = (1,0,0)
  Length = 1.2
  Length2 = 5
  Profile = -> Sketch003
  ReferenceAxis = -> Sketch003 [N_Axis]
  Refine = true
  Suppressed = false
  Type = 0
FEATURE [PartDesign::Chamfer] Chamfer
  Angle = 45
  Base = -> Pocket003 [Edge123]
  BaseFeature = -> Pocket003
  ChamferType = 0
  FlipDirection = false
  Refine = true
  Size = 2.59
  Size2 = 1
  SupportTransform = false
  Suppressed = false
  UseAllEdges = false
FEATURE [Sketcher::SketchObject] Sketch004
  ArcFitTolerance = 1e-06
  AttachmentSupport = -> [Chamfer]
  ExternalGeometry = -> [Chamfer]
  FullyConstrained = true
  MakeInternals = false
  MapMode = 5
  Placement = pos=(14.25,0,0) rot=(0.57735,0.57735,0.57735;2.0944rad)
  sketch-geometry (3):
    g0: ArcOfCircle CenterX=4 CenterY=42 CenterZ=0 NormalX=0 NormalY=0 NormalZ=1 AngleXU=0 Radius=8 StartAngle=3.14159 EndAngle=4.71239
    g1: LineSegment StartX=-4 StartY=42 StartZ=0 EndX=-4 EndY=34 EndZ=0
    g2: LineSegment StartX=-4 StartY=34 StartZ=0 EndX=4 EndY=34 EndZ=0
  constraints (7):
    c: Tangent(g0,g-3) = 1.5708
    c: Tangent(g0,g-4) = 1.5708
    c: Radius(g0) = 8
    c: Coincident(g1,g0)
    c: Coincident(g1,g-4)
    c: Coincident(g2,g1)
    c: Coincident(g2,g0)
FEATURE [PartDesign::Pocket] Pocket004
  BaseFeature = -> Chamfer
  Direction = (-1,0,0)
  Length = 0
  Length2 = 5
  Profile = -> Sketch004
  ReferenceAxis = -> Sketch004 [N_Axis]
  Refine = true
  Suppressed = false
  Type = 3
  UpToFace = -> Chamfer [Face21]
FEATURE [Sketcher::SketchObject] Sketch005
  ArcFitTolerance = 1e-06
  AttachmentSupport = -> [Pocket004]
  ExternalGeometry = -> [Pocket004,DatumLine]
  FullyConstrained = true
  MakeInternals = false
  MapMode = 5
  Placement = pos=(14.25,0,0) rot=(0.57735,0.57735,0.57735;2.0944rad)
  sketch-geometry (5):
    g0: LineSegment StartX=-4 StartY=42 StartZ=0 EndX=-4 EndY=48 EndZ=0
    g1: LineSegment StartX=-4 StartY=48 StartZ=0 EndX=0 EndY=48 EndZ=0
    g2: LineSegment StartX=0 StartY=48 StartZ=0 EndX=0 EndY=44.6816 EndZ=0
    g3: LineSegment StartX=-4 StartY=42 StartZ=0 EndX=-2.55553 EndY=42 EndZ=0
    g4: ArcOfCircle CenterX=4.505 CenterY=37.83 CenterZ=0 NormalX=0 NormalY=0 NormalZ=1 AngleXU=0 Radius=8.2 StartAngle=2.15243 EndAngle=2.60811
  constraints (13):
    c: Coincident(g0,g-3)
    c: Coincident(g0,g-4)
    c: Coincident(g1,g0)
    c: Horizontal(g1)
    c: Coincident(g2,g1)
    c: Vertical(g2)
    c: Coincident(g3,g0)
    c: Horizontal(g3)
    c: Coincident(g4,g-5)
    c: Coincident(g4,g2)
    c: Coincident(g4,g3)
    c: Radius(g4) = 8.2
    c: Distance(g1,g-4) = 16
FEATURE [PartDesign::Pad] Pad005
  BaseFeature = -> Pocket004
  Direction = (1,0,0)
  Length = 10
  Length2 = 10
  Profile = -> Sketch005
  ReferenceAxis = -> Sketch005 [N_Axis]
  Refine = true
  Suppressed = false
  Type = 3
  UpToFace = -> Pocket004 [Face18]
FEATURE [Sketcher::SketchObject] Sketch006
  ArcFitTolerance = 1e-06
  AttachmentSupport = -> [Pad005]
  ExternalGeometry = -> [Pad005]
  FullyConstrained = true
  MakeInternals = false
  MapMode = 5
  Placement = pos=(3.3,0,0) rot=(0.57735,0.57735,0.57735;2.0944rad)
  sketch-geometry (4):
    g0: LineSegment StartX=-4 StartY=42 StartZ=0 EndX=-4 EndY=41 EndZ=0
    g1: LineSegment StartX=-4 StartY=42 StartZ=0 EndX=-2.55553 EndY=42 EndZ=0
    g2: LineSegment StartX=-4 StartY=41 StartZ=0 EndX=-3.05748 EndY=41 EndZ=0
    g3: ArcOfCircle CenterX=4.505 CenterY=37.83 CenterZ=0 NormalX=0 NormalY=0 NormalZ=1 AngleXU=0 Radius=8.2 StartAngle=2.60811 EndAngle=2.74467
  constraints (10):
    c: Coincident(g0,g-4)
    c: PointOnObject(g0,g-3)
    c: Coincident(g1,g0)
    c: Coincident(g1,g-5)
    c: Coincident(g2,g0)
    c: Horizontal(g2)
    c: Coincident(g3,g1)
    c: Coincident(g3,g2)
    c: Distance(g0,g0) = 1
    c: Coincident(g3,g-5)
FEATURE [PartDesign::Pad] Pad006
  BaseFeature = -> Pad005
  Direction = (1,0,0)
  Length = 10
  Length2 = 10
  Profile = -> Sketch006
  ReferenceAxis = -> Sketch006 [N_Axis]
  Refine = true
  Suppressed = false
  Type = 3
  UpToFace = -> Pad005 [Face16]
FEATURE [PartDesign::Body] Body  label="k1_joint_left"
  AllowCompound = false
  BaseFeature = -> Part__Feature
  Group = -> [BaseFeature,DatumLine,Pocket,Pocket001,Pad,Pad001,Pad002,Sketch,Pocket002,Sketch001,Pad003,Sketch002,Pad004,Sketch003,Pocket003,Chamfer,Sketch004,Pocket004,Sketch005,Pad005,Sketch006,Pad006]
  Origin = -> Origin
  Tip = -> Pad006
FEATURE [App::Link] Link  label="mgn12h_block_link"
  LinkPlacement = pos=(29.9999,9.5,43.2) rot=(0,1,0;1.5708rad)
  LinkedObject = -> <external cad_mgn12h_block.FCStd>#Body
  Placement = pos=(29.9999,9.5,43.2) rot=(0,1,0;1.5708rad)
FEATURE [App::Link] Link001  label="powge_pulley_top_link"
  LinkPlacement = pos=(14.75,4.505,37.83) rot=(0,1,0;1.5708rad)
  LinkedObject = -> <external cad_powge_pulley.FCStd>#Part
  Placement = pos=(14.75,4.505,37.83) rot=(0,1,0;1.5708rad)
FEATURE [App::Link] Link002  label="powge_pulley_bottom_link"
  LinkPlacement = pos=(3.8,18,24) rot=(0,1,0;1.5708rad)
  LinkedObject = -> <external cad_powge_pulley.FCStd>#Part
  Placement = pos=(3.8,18,24) rot=(0,1,0;1.5708rad)
FEATURE [App::Part] Part  label="k1_joint_left_part"
  Group = -> [Part__Feature,Body,Link,Link001,Link002]
  Origin = -> Origin001
  Placement = pos=(0,0,0) rot=(0.57735,-0.57735,0.57735;2.0944rad)
---- part k1_joint_right.FCStd = doc fcstd_f1109201a2f2 ----
FCSTD DOCUMENT  (FreeCAD 1.0R38641 +468 (Git))
Label: k1_joint_right
License: All rights reserved
LicenseURL: https://en.wikipedia.org/wiki/All_rights_reserved
objects: Sketcher::SketchObject×8, PartDesign::Pad×7, PartDesign::Pocket×6, App::Link×3, Part::Feature×1, PartDesign::FeatureBase×1, PartDesign::Line×1, PartDesign::Chamfer×1, PartDesign::Body×1, App::Part×1
note: 63 computed .brp shape members not serialized (recipe doc carries the construction recipe); baked Part::Feature solids carry a one-line shape summary decoded from their .brp
EXTERNAL_REF file=cad_powge_pulley.FCStd obj=Part
EXTERNAL_REF file=cad_mgn12h_block.FCStd obj=Body

FEATURE [Part::Feature] Part__Feature  label="step"
  shape: bbox 32.5 x 27 x 53.87 mm, 57 faces (baked)
FEATURE [PartDesign::FeatureBase] BaseFeature
  BaseFeature = -> Part__Feature
  Suppressed = false
FEATURE [PartDesign::Line] DatumLine  label="front_idler_axis"
  AttacherType = Attacher::AttachEngineLine
  AttachmentOffset = pos=(-1.495,0,0) rot=(0,0,1;0rad)
  AttachmentSupport = -> [BaseFeature]
  Length = 20
  MapMode = 19
  Placement = pos=(29.9999,-4.505,37.83) rot=(0.57735,-0.57735,-0.57735;2.0944rad)
  ResizeMode = 0
FEATURE [Sketcher::SketchObject] Sketch
  ArcFitTolerance = 1e-06
  AttachmentSupport = -> [BaseFeature]
  ExternalGeometry = -> [BaseFeature]
  FullyConstrained = true
  MakeInternals = false
  MapMode = 5
  Placement = pos=(3.3,0,0) rot=(0.57735,0.57735,0.57735;2.0944rad)
  sketch-geometry (6):
    g0: LineSegment StartX=-17 StartY=48 StartZ=0 EndX=-16 EndY=48 EndZ=0
    g1: LineSegment StartX=-17 StartY=48 StartZ=0 EndX=-17 EndY=35 EndZ=0
    g2: LineSegment StartX=-9 StartY=27 StartZ=0 EndX=-8 EndY=27 EndZ=0
    g3: LineSegment StartX=-16 StartY=48 StartZ=0 EndX=-16 EndY=35 EndZ=0
    g4: ArcOfCircle CenterX=-9 CenterY=35 CenterZ=0 NormalX=0 NormalY=0 NormalZ=1 AngleXU=0 Radius=8 StartAngle=3.14159 EndAngle=4.71239
    g5: ArcOfCircle CenterX=-8 CenterY=35 CenterZ=0 NormalX=0 NormalY=0 NormalZ=1 AngleXU=0 Radius=8 StartAngle=3.14159 EndAngle=4.71239
  constraints (15):
    c: Coincident(g0,g-4)
    c: PointOnObject(g0,g-4)
    c: Coincident(g3,g0)
    c: Vertical(g3)
    c: PointOnObject(g2,g-6)
    c: Distance(g0,g0) = 1
    c: Coincident(g2,g-6)
    c: Equal(g1,g3)
    c: Coincident(g1,g-5)
    c: Coincident(g4,g1)
    c: Coincident(g4,g2)
    c: Radius(g4) = 8
    c: Tangent(g5,g2) = -1.5708
    c: Tangent(g5,g3) = -1.5708
    c: Coincident(g0,g1)
FEATURE [PartDesign::Pad] Pad
  BaseFeature = -> BaseFeature
  Direction = (1,0,0)
  Length = 10
  Length2 = 10
  Profile = -> Sketch
  ReferenceAxis = -> Sketch [N_Axis]
  Refine = true
  Suppressed = false
  Type = 3
  UpToFace = -> BaseFeature [Face15]
FEATURE [PartDesign::Pocket] Pocket
  BaseFeature = -> Pad
  Direction = (-1,0,0)
  Length = 0
  Length2 = 5
  Profile = -> Pad [Face49]
  Refine = true
  Suppressed = false
  Type = 3
  UpToFace = -> Pad [Face23]
FEATURE [PartDesign::Pocket] Pocket001
  BaseFeature = -> Pocket
  Direction = (1,0,0)
  Length = 0
  Length2 = 5
  Profile = -> Pocket [Face29]
  Refine = true
  Suppressed = false
  Type = 3
  UpToFace = -> Pocket [Face15]
FEATURE [PartDesign::Pocket] Pocket002
  BaseFeature = -> Pocket001
  Direction = (-1,0,0)
  Length = 0
  Length2 = 5
  Profile = -> Pocket001 [Face46]
  Refine = true
  Suppressed = false
  Type = 3
  UpToFace = -> Pocket001 [Face16]
FEATURE [PartDesign::Pad] Pad001
  BaseFeature = -> Pocket002
  Direction = (1,0,0)
  Length = 10
  Length2 = 10
  Profile = -> Pocket002 [Edge74]
  Refine = true
  Suppressed = false
  Type = 3
  UpToFace = -> Pocket002 [Face53]
FEATURE [PartDesign::Pad] Pad002
  BaseFeature = -> Pad001
  Direction = (1,0,0)
  Length = 10
  Length2 = 10
  Profile = -> Pad001 [Edge52]
  Refine = true
  Suppressed = false
  Type = 3
  UpToFace = -> Pad001 [Face10]
FEATURE [Sketcher::SketchObject] Sketch001
  ArcFitTolerance = 1e-06
  AttachmentSupport = -> [Pad002]
  ExternalGeometry = -> [DatumLine]
  FullyConstrained = true
  MakeInternals = false
  MapMode = 5
  Placement = pos=(-2.5,0,0) rot=(0.57735,-0.57735,-0.57735;2.0944rad)
  sketch-geometry (1):
    g0: Circle CenterX=4.505 CenterY=37.83 CenterZ=0 NormalX=0 NormalY=0 NormalZ=1 AngleXU=0 Radius=1.9
  constraints (2):
    c: Coincident(g0,g-3)
    c: Diameter(g0) = 3.8
FEATURE [PartDesign::Pocket] Pocket003
  BaseFeature = -> Pad002
  Direction = (1,0,0)
  Length = 5
  Length2 = 5
  Profile = -> Sketch001
  ReferenceAxis = -> Sketch001 [N_Axis]
  Refine = true
  Suppressed = false
  Type = 1
FEATURE [Sketcher::SketchObject] Sketch002
  ArcFitTolerance = 1e-06
  AttachmentSupport = -> [Pocket003]
  ExternalGeometry = -> [DatumLine]
  FullyConstrained = true
  MakeInternals = false
  MapMode = 5
  Placement = pos=(14.8,0,0) rot=(0.57735,-0.57735,-0.57735;2.0944rad)
  sketch-geometry (2):
    g0: Circle CenterX=4.505 CenterY=37.83 CenterZ=0 NormalX=0 NormalY=0 NormalZ=1 AngleXU=0 Radius=1.9
    g1: Circle CenterX=4.505 CenterY=37.83 CenterZ=0 NormalX=0 NormalY=0 NormalZ=1 AngleXU=0 Radius=3
  constraints (4):
    c: Coincident(g0,g-3)
    c: Coincident(g1,g0)
    c: Diameter(g1) = 6
    c: Diameter(g0) = 3.8
FEATURE [PartDesign::Pad] Pad003
  BaseFeature = -> Pocket003
  Direction = (-1,0,0)
  Length = 0.5
  Length2 = 10
  Profile = -> Sketch002
  ReferenceAxis = -> Sketch002 [N_Axis]
  Refine = true
  Suppressed = false
  Type = 0
FEATURE [Sketcher::SketchObject] Sketch003
  ArcFitTolerance = 1e-06
  AttachmentSupport = -> [Pad003]
  ExternalGeometry = -> [DatumLine]
  FullyConstrained = true
  MakeInternals = false
  MapMode = 5
  Placement = pos=(3.3,0,0) rot=(0.57735,0.57735,0.57735;2.0944rad)
  sketch-geometry (2):
    g0: Circle CenterX=-4.505 CenterY=37.83 CenterZ=0 NormalX=0 NormalY=0 NormalZ=1 AngleXU=0 Radius=3
    g1: Circle CenterX=-4.505 CenterY=37.83 CenterZ=0 NormalX=0 NormalY=0 NormalZ=1 AngleXU=0 Radius=1.9
  constraints (4):
    c: Coincident(g0,g-3)
    c: Coincident(g1,g0)
    c: Diameter(g0) = 6
    c: Diameter(g1) = 3.8
FEATURE [PartDesign::Pad] Pad004
  BaseFeature = -> Pad003
  Direction = (1,0,0)
  Length = 0.5
  Length2 = 10
  Profile = -> Sketch003
  ReferenceAxis = -> Sketch003 [N_Axis]
  Refine = true
  Suppressed = false
  Type = 0
FEATURE [Sketcher::SketchObject] Sketch004
  ArcFitTolerance = 1e-06
  AttachmentSupport = -> [Pad004]
  ExternalGeometry = -> [DatumLine]
  FullyConstrained = true
  MakeInternals = false
  MapMode = 5
  Placement = pos=(-2.5,0,0) rot=(0.57735,-0.57735,-0.57735;2.0944rad)
  sketch-geometry (1):
    g0: Circle CenterX=4.505 CenterY=37.83 CenterZ=0 NormalX=0 NormalY=0 NormalZ=1 AngleXU=0 Radius=4.5
  constraints (2):
    c: Coincident(g0,g-3)
    c: Diameter(g0) = 9
FEATURE [PartDesign::Pocket] Pocket004
  BaseFeature = -> Pad004
  Direction = (1,0,0)
  Length = 1.2
  Length2 = 5
  Profile = -> Sketch004
  ReferenceAxis = -> Sketch004 [N_Axis]
  Refine = true
  Suppressed = false
  Type = 0
FEATURE [PartDesign::Chamfer] Chamfer
  Angle = 45
  Base = -> Pocket004 [Edge91]
  BaseFeature = -> Pocket004
  ChamferType = 0
  FlipDirection = false
  Refine = true
  Size = 2.59
  Size2 = 1
  SupportTransform = false
  Suppressed = false
  UseAllEdges = false
FEATURE [Sketcher::SketchObject] Sketch005
  ArcFitTolerance = 1e-06
  AttachmentSupport = -> [Chamfer]
  ExternalGeometry = -> [Chamfer]
  FullyConstrained = true
  MakeInternals = false
  MapMode = 5
  Placement = pos=(14.8,0,0) rot=(0.57735,-0.57735,-0.57735;2.0944rad)
  sketch-geometry (3):
    g0: ArcOfCircle CenterX=4 CenterY=42 CenterZ=0 NormalX=0 NormalY=0 NormalZ=1 AngleXU=0 Radius=8 StartAngle=3.14159 EndAngle=4.71239
    g1: LineSegment StartX=-4 StartY=34 StartZ=0 EndX=4 EndY=34 EndZ=0
    g2: LineSegment StartX=-4 StartY=34 StartZ=0 EndX=-4 EndY=42 EndZ=0
  constraints (7):
    c: Tangent(g0,g-3) = -1.5708
    c: Tangent(g0,g-4) = 1.5708
    c: Radius(g0) = 8
    c: Coincident(g1,g-4)
    c: Coincident(g1,g0)
    c: Coincident(g2,g1)
    c: Tangent(g2,g0) = 1.5708
FEATURE [PartDesign::Pocket] Pocket005
  BaseFeature = -> Chamfer
  Direction = (1,0,0)
  Length = 0
  Length2 = 5
  Profile = -> Sketch005
  ReferenceAxis = -> Sketch005 [N_Axis]
  Refine = true
  Suppressed = false
  Type = 3
  UpToFace = -> Chamfer [Face23]
FEATURE [Sketcher::SketchObject] Sketch006
  ArcFitTolerance = 1e-06
  AttachmentSupport = -> [Pocket005]
  ExternalGeometry = -> [Pocket005,DatumLine]
  FullyConstrained = true
  MakeInternals = false
  MapMode = 5
  Placement = pos=(3.3,0,0) rot=(0.57735,0.57735,0.57735;2.0944rad)
  sketch-geometry (5):
    g0: LineSegment StartX=0 StartY=48 StartZ=0 EndX=4 EndY=48 EndZ=0
    g1: LineSegment StartX=4 StartY=48 StartZ=0 EndX=4 EndY=42 EndZ=0
    g2: LineSegment StartX=0 StartY=48 StartZ=0 EndX=0 EndY=44.6816 EndZ=0
    g3: LineSegment StartX=4 StartY=42 StartZ=0 EndX=2.55553 EndY=42 EndZ=0
    g4: ArcOfCircle CenterX=-4.505 CenterY=37.83 CenterZ=0 NormalX=0 NormalY=0 NormalZ=1 AngleXU=0 Radius=8.2 StartAngle=0.533484 EndAngle=0.989162
  constraints (13):
    c: PointOnObject(g0,g-3)
    c: Coincident(g0,g-4)
    c: Coincident(g1,g0)
    c: Coincident(g2,g0)
    c: Vertical(g2)
    c: Coincident(g3,g1)
    c: Horizontal(g3)
    c: Distance(g0,g-3) = 16
    c: Coincident(g4,g-5)
    c: Coincident(g4,g2)
    c: Coincident(g4,g3)
    c: Radius(g4) = 8.2
    c: Coincident(g1,g-6)
FEATURE [PartDesign::Pad] Pad005
  BaseFeature = -> Pocket005
  Direction = (1,0,0)
  Length = 10
  Length2 = 10
  Profile = -> Sketch006
  ReferenceAxis = -> Sketch006 [N_Axis]
  Refine = true
  Suppressed = false
  Type = 3
  UpToFace = -> Pocket005 [Face22]
FEATURE [Sketcher::SketchObject] Sketch007
  ArcFitTolerance = 1e-06
  AttachmentSupport = -> [Pad005]
  ExternalGeometry = -> [Pad005]
  FullyConstrained = true
  MakeInternals = false
  MapMode = 5
  Placement = pos=(3.3,0,0) rot=(0.57735,0.57735,0.57735;2.0944rad)
  sketch-geometry (4):
    g0: LineSegment StartX=4 StartY=42 StartZ=0 EndX=4 EndY=41 EndZ=0
    g1: LineSegment StartX=4 StartY=42 StartZ=0 EndX=2.55553 EndY=42 EndZ=0
    g2: LineSegment StartX=4 StartY=41 StartZ=0 EndX=3.05748 EndY=41 EndZ=0
    g3: ArcOfCircle CenterX=-4.505 CenterY=37.83 CenterZ=0 NormalX=0 NormalY=0 NormalZ=1 AngleXU=0 Radius=8.2 StartAngle=0.396926 EndAngle=0.533484
  constraints (10):
    c: Coincident(g0,g-4)
    c: PointOnObject(g0,g-4)
    c: Coincident(g1,g0)
    c: Coincident(g1,g-5)
    c: Coincident(g2,g0)
    c: Horizontal(g2)
    c: Coincident(g3,g-5)
    c: Coincident(g3,g1)
    c: Coincident(g3,g2)
    c: Distance(g0,g0) = 1
FEATURE [PartDesign::Pad] Pad006
  BaseFeature = -> Pad005
  Direction = (1,0,0)
  Length = 10
  Length2 = 10
  Profile = -> Sketch007
  ReferenceAxis = -> Sketch007 [N_Axis]
  Refine = true
  Suppressed = false
  Type = 3
  UpToFace = -> Pad005 [Face3]
FEATURE [PartDesign::Body] Body  label="k1_joint_right"
  AllowCompound = false
  BaseFeature = -> Part__Feature
  Group = -> [BaseFeature,DatumLine,Sketch,Pad,Pocket,Pocket001,Pocket002,Pad001,Pad002,Sketch001,Pocket003,Sketch002,Pad003,Sketch003,Pad004,Sketch004,Pocket004,Chamfer,Sketch005,Pocket005,Sketch006,Pad005,Sketch007,Pad006]
  Origin = -> Origin
  Tip = -> Pad006
FEATURE [App::Link] Link  label="cad_powge_pulley_top_link"
  LinkPlacement = pos=(14.75,-18,24) rot=(0,1,0;1.5708rad)
  LinkedObject = -> <external cad_powge_pulley.FCStd>#Part
  Placement = pos=(14.75,-18,24) rot=(0,1,0;1.5708rad)
FEATURE [App::Link] Link001  label="cad_powge_pulley_bottom_link"
  LinkPlacement = pos=(3.8,-4.505,37.83) rot=(0,1,0;1.5708rad)
  LinkedObject = -> <external cad_powge_pulley.FCStd>#Part
  Placement = pos=(3.8,-4.505,37.83) rot=(0,1,0;1.5708rad)
FEATURE [App::Link] Link002  label="mgn12_block_link"
  LinkPlacement = pos=(29.9999,-9.5,43.2) rot=(0,1,0;1.5708rad)
  LinkedObject = -> <external cad_mgn12h_block.FCStd>#Body
  Placement = pos=(29.9999,-9.5,43.2) rot=(0,1,0;1.5708rad)
FEATURE [App::Part] Part  label="k1_joint_right_part"
  Group = -> [Part__Feature,Body,Link,Link001,Link002]
  Origin = -> Origin001
  Placement = pos=(0,0,0) rot=(0.57735,-0.57735,0.57735;2.0944rad)
---- part k1_motor_mount_couplers_stock_left.FCStd = doc fcstd_677c1ffc108a ----
FCSTD DOCUMENT  (FreeCAD 1.0R38641 +468 (Git))
Label: k1_motor_mount_couplers_stock_left
License: All rights reserved
LicenseURL: https://en.wikipedia.org/wiki/All_rights_reserved
objects: App::Link×9, PartDesign::Pad×3, PartDesign::Pocket×3, Sketcher::SketchObject×2, Part::Feature×1, PartDesign::FeatureBase×1, PartDesign::Line×1, PartDesign::Body×1, App::Part×1
note: 27 computed .brp shape members not serialized (recipe doc carries the construction recipe); baked Part::Feature solids carry a one-line shape summary decoded from their .brp
EXTERNAL_REF file=cad_powge_pulley.FCStd obj=Part
EXTERNAL_REF file=cad_mf95zz.FCStd obj=Body
EXTERNAL_REF file=cad_motor_shaft_55mm.FCStd obj=Part__Feature
EXTERNAL_REF file=cad_20T_15mm_pulley.FCStd obj=Part
EXTERNAL_REF file=cad_nema17_42_60.FCStd obj=COMPOUND049
EXTERNAL_REF file=cad_diaphragm_coupler.FCStd obj=_764K239_NO_THREADS_Servomotor_Precision_Flexible_Shaft_Coupling013
EXTERNAL_REF file=cad_m4_35mm.FCStd obj=Part__Feature

FEATURE [Part::Feature] Part__Feature  label="step"
  shape: bbox 73.5 x 47.7 x 110.9 mm, 153 faces (baked)
FEATURE [PartDesign::FeatureBase] BaseFeature
  BaseFeature = -> Part__Feature
  Suppressed = false
FEATURE [App::Link] Link  label="cad_powge_pulley_top_link"
  LinkPlacement = pos=(14.1406,100.078,20.85) rot=(0,0,1;0rad)
  LinkedObject = -> <external cad_powge_pulley.FCStd>#Part
  Placement = pos=(14.1406,100.078,20.85) rot=(0,0,1;0rad)
FEATURE [App::Link] Link001  label="cad_powge_pulley_bottom_link"
  LinkPlacement = pos=(14.1406,100.078,9.7) rot=(0,0,1;0rad)
  LinkedObject = -> <external cad_powge_pulley.FCStd>#Part
  Placement = pos=(14.1406,100.078,9.7) rot=(0,0,1;0rad)
FEATURE [App::Link] Link002  label="cad_mf95zz_top_link"
  LinkPlacement = pos=(29.6406,84.5783,37.2) rot=(0,1,0;3.14159rad)
  LinkedObject = -> <external cad_mf95zz.FCStd>#Body
  Placement = pos=(29.6406,84.5783,37.2) rot=(0,1,0;3.14159rad)
FEATURE [App::Link] Link003  label="cad_mf95zz_bottom_link"
  LinkPlacement = pos=(29.6406,84.5783,-4.4) rot=(0,0,1;3.14159rad)
  LinkedObject = -> <external cad_mf95zz.FCStd>#Body
  Placement = pos=(29.6406,84.5783,-4.4) rot=(0,0,1;3.14159rad)
FEATURE [App::Link] Link004  label="cad_motor_shaft_55mm_link"
  LinkPlacement = pos=(370.445,-290.422,175.11) rot=(0,0,1;0rad)
  LinkedObject = -> <external cad_motor_shaft_55mm.FCStd>#Part__Feature
  Placement = pos=(370.445,-290.422,175.11) rot=(0,0,1;0rad)
FEATURE [App::Link] Link005  label="cad_20T_15mm_pulley_link"
  LinkPlacement = pos=(117.263,15.5011,1.55198) rot=(0,1,0;3.14159rad)
  LinkedObject = -> <external cad_20T_15mm_pulley.FCStd>#Part
  Placement = pos=(117.263,15.5011,1.55198) rot=(0,1,0;3.14159rad)
FEATURE [App::Link] Link006  label="cad_nema17_42_60_link"
  LinkPlacement = pos=(29.6406,84.5783,-79.702) rot=(0,0,1;0rad)
  LinkedObject = -> <external cad_nema17_42_60.FCStd>#COMPOUND049
  Placement = pos=(29.6406,84.5783,-79.702) rot=(0,0,1;0rad)
FEATURE [App::Link] Link007  label="cad_diaphragm_coupler_5_5_link"
  LinkPlacement = pos=(370.37,-290.416,168.405) rot=(0,0,1;0rad)
  LinkedObject = -> <external cad_diaphragm_coupler.FCStd>#_764K239_NO_THREADS_Servomotor_Precision_Flexible_Shaft_Coupling013
  Placement = pos=(370.37,-290.416,168.405) rot=(0,0,1;0rad)
FEATURE [App::Link] Link008  label="cad_m4_35mm_link"
  LinkPlacement = pos=(14.1406,100.078,0.376278) rot=(0,0,1;0rad)
  LinkedObject = -> <external cad_m4_35mm.FCStd>#Part__Feature
  Placement = pos=(14.1406,100.078,0.376278) rot=(0,0,1;0rad)
FEATURE [PartDesign::Line] DatumLine  label="rails_mount"
  AttacherType = Attacher::AttachEngineLine
  AttachmentOffset = pos=(-0.22,-2.5,0) rot=(0,0,1;0rad)
  AttachmentSupport = -> [BaseFeature]
  Length = 20
  MapMode = 19
  Placement = pos=(72.5256,986.528,40.945) rot=(0,0,1;0rad)
  ResizeMode = 0
FEATURE [PartDesign::Pad] Pad
  BaseFeature = -> BaseFeature
  Direction = (4.42e-14,0,-1)
  Length = 10
  Length2 = 10
  Profile = -> BaseFeature [Face49]
  Refine = true
  Suppressed = false
  Type = 3
  UpToFace = -> BaseFeature [Face17]
FEATURE [PartDesign::Pad] Pad001
  BaseFeature = -> Pad
  Direction = (0,0,1)
  Length = 10
  Length2 = 10
  Profile = -> Pad [Edge129]
  Refine = true
  Suppressed = false
  Type = 3
  UpToFace = -> Pad [Face140]
FEATURE [Sketcher::SketchObject] Sketch
  ArcFitTolerance = 1e-06
  AttachmentSupport = -> [Pad001]
  ExternalGeometry = -> [DatumLine]
  FullyConstrained = true
  MakeInternals = false
  MapMode = 5
  Placement = pos=(0,-9.3e-15,40.945) rot=(0,0,1;0rad)
  sketch-geometry (1):
    g0: Circle CenterX=72.5256 CenterY=986.528 CenterZ=0 NormalX=0 NormalY=0 NormalZ=1 AngleXU=0 Radius=1.6
  constraints (2):
    c: Coincident(g0,g-3)
    c: Diameter(g0) = 3.2
FEATURE [PartDesign::Pocket] Pocket  label="mount_hole"
  BaseFeature = -> Pad001
  Direction = (0,0,-1)
  Length = 10
  Length2 = 5
  Profile = -> Sketch
  ReferenceAxis = -> Sketch [N_Axis]
  Refine = true
  Suppressed = false
  Type = 0
FEATURE [PartDesign::Pocket] Pocket001  label="move_left_wall"
  BaseFeature = -> Pocket
  Direction = (-1,0,0)
  Length = 0.225
  Length2 = 5
  Profile = -> Pocket [Face18]
  Refine = true
  Suppressed = false
  Type = 0
FEATURE [PartDesign::Pad] Pad002  label="move_right_wall"
  BaseFeature = -> Pocket001
  Direction = (-1,0,0)
  Length = 0.215
  Length2 = 10
  Profile = -> Pocket001 [Face9]
  Refine = true
  Suppressed = false
  Type = 0
FEATURE [Sketcher::SketchObject] Sketch002
  ArcFitTolerance = 1e-06
  AttachmentSupport = -> [Pad002]
  ExternalGeometry = -> [DatumLine]
  FullyConstrained = true
  MakeInternals = false
  MapMode = 5
  Placement = pos=(-6.26e-13,-1.774e-13,32.8) rot=(1,0,0;3.14159rad)
  sketch-geometry (1):
    g0: Circle CenterX=72.5256 CenterY=-986.528 CenterZ=0 NormalX=0 NormalY=0 NormalZ=1 AngleXU=0 Radius=1.95
  constraints (2):
    c: Coincident(g0,g-3)
    c: Diameter(g0) = 3.9
FEATURE [PartDesign::Pocket] Pocket002  label="rail_heat_insert"
  BaseFeature = -> Pad002
  Direction = (-1.91e-14,-5.4e-15,1)
  Length = 5.1
  Length2 = 5
  Profile = -> Sketch002
  ReferenceAxis = -> Sketch002 [N_Axis]
  Refine = true
  Suppressed = false
  Type = 0
FEATURE [PartDesign::Body] Body  label="k1_motor_mount_couplers_stock_left"
  AllowCompound = false
  BaseFeature = -> Part__Feature
  Group = -> [BaseFeature,DatumLine,Pad,Pad001,Sketch,Pocket,Pocket001,Pad002,Sketch002,Pocket002]
  Origin = -> Origin
  Placement = pos=(-50,-900,0) rot=(0,0,1;0rad)
  Tip = -> Pocket002
FEATURE [App::Part] Part  label="k1_motor_mount_couplers_stock_left_part"
  Group = -> [Part__Feature,Body,Link,Link001,Link002,Link003,Link004,Link005,Link006,Link007,Link008]
  Origin = -> Origin001
---- part k1_motor_mount_couplers_stock_right.FCStd = doc fcstd_f802b26615a8 ----
FCSTD DOCUMENT  (FreeCAD 1.0R38641 +468 (Git))
Label: k1_motor_mount_couplers_stock_right
License: All rights reserved
LicenseURL: https://en.wikipedia.org/wiki/All_rights_reserved
objects: App::Link×9, PartDesign::Pad×3, PartDesign::Pocket×3, Sketcher::SketchObject×2, Part::Feature×1, PartDesign::FeatureBase×1, PartDesign::Line×1, PartDesign::Body×1, App::Part×1
note: 27 computed .brp shape members not serialized (recipe doc carries the construction recipe); baked Part::Feature solids carry a one-line shape summary decoded from their .brp
EXTERNAL_REF file=cad_powge_pulley.FCStd obj=Part
EXTERNAL_REF file=cad_20T_15mm_pulley.FCStd obj=Part
EXTERNAL_REF file=cad_mf95zz.FCStd obj=Body
EXTERNAL_REF file=cad_diaphragm_coupler.FCStd obj=_764K239_NO_THREADS_Servomotor_Precision_Flexible_Shaft_Coupling013
EXTERNAL_REF file=cad_nema17_42_60.FCStd obj=COMPOUND049
EXTERNAL_REF file=cad_motor_shaft_55mm.FCStd obj=Part__Feature
EXTERNAL_REF file=cad_m4_35mm.FCStd obj=Part__Feature

FEATURE [Part::Feature] Part__Feature  label="step"
  shape: bbox 73.5 x 47.7 x 110.9 mm, 157 faces (baked)
FEATURE [PartDesign::FeatureBase] BaseFeature
  BaseFeature = -> Part__Feature
  Suppressed = false
FEATURE [App::Link] Link  label="cad_powge_pulley_top_link"
  LinkPlacement = pos=(94.1406,100.078,88.8) rot=(0,0,1;0rad)
  LinkedObject = -> <external cad_powge_pulley.FCStd>#Part
  Placement = pos=(94.1406,100.078,88.8) rot=(0,0,1;0rad)
FEATURE [App::Link] Link001  label="cad_powge_pulley_bottom_link"
  LinkPlacement = pos=(94.1406,100.078,77.7) rot=(0,0,1;0rad)
  LinkedObject = -> <external cad_powge_pulley.FCStd>#Part
  Placement = pos=(94.1406,100.078,77.7) rot=(0,0,1;0rad)
FEATURE [App::Link] Link002  label="cad_20T_15mm_pulley_link"
  LinkPlacement = pos=(-8.98206,15.5009,105.208) rot=(0,-1.00667,0;0rad)
  LinkedObject = -> <external cad_20T_15mm_pulley.FCStd>#Part
  Placement = pos=(-8.98206,15.5009,105.208) rot=(0,-1.00667,0;0rad)
FEATURE [App::Link] Link003  label="cad_mf95zz_top_link"
  LinkPlacement = pos=(78.6406,84.5783,105.2) rot=(0,1,0;3.14159rad)
  LinkedObject = -> <external cad_mf95zz.FCStd>#Body
  Placement = pos=(78.6406,84.5783,105.2) rot=(0,1,0;3.14159rad)
FEATURE [App::Link] Link004  label="cad_mf95zz_bottom_link"
  LinkPlacement = pos=(78.6406,84.5783,63.6) rot=(0,0,1;0rad)
  LinkedObject = -> <external cad_mf95zz.FCStd>#Body
  Placement = pos=(78.6406,84.5783,63.6) rot=(0,0,1;0rad)
FEATURE [App::Link] Link005  label="cad_diaphragm_coupler_5_5_link001"
  LinkPlacement = pos=(419.37,-290.416,235.548) rot=(0,0,1;0rad)
  LinkedObject = -> <external cad_diaphragm_coupler.FCStd>#_764K239_NO_THREADS_Servomotor_Precision_Flexible_Shaft_Coupling013
  Placement = pos=(419.37,-290.416,235.548) rot=(0,0,1;0rad)
FEATURE [App::Link] Link006  label="cad_nema17_42_60_link"
  LinkPlacement = pos=(78.6406,84.5783,-11.702) rot=(0,0,1;3.14159rad)
  LinkedObject = -> <external cad_nema17_42_60.FCStd>#COMPOUND049
  Placement = pos=(78.6406,84.5783,-11.702) rot=(0,0,1;3.14159rad)
FEATURE [App::Link] Link007  label="cad_motor_shaft_55mm_link"
  LinkPlacement = pos=(419.445,-290.422,242.202) rot=(0,0,1;0rad)
  LinkedObject = -> <external cad_motor_shaft_55mm.FCStd>#Part__Feature
  Placement = pos=(419.445,-290.422,242.202) rot=(0,0,1;0rad)
FEATURE [App::Link] Link008  label="cad_m4_35mm_link"
  LinkPlacement = pos=(94.1406,100.078,68.3263) rot=(0,0,1;0rad)
  LinkedObject = -> <external cad_m4_35mm.FCStd>#Part__Feature
  Placement = pos=(94.1406,100.078,68.3263) rot=(0,0,1;0rad)
FEATURE [PartDesign::Line] DatumLine  label="rails_mount"
  AttacherType = Attacher::AttachEngineLine
  AttachmentOffset = pos=(0.22,-2.5,0) rot=(0,0,1;0rad)
  AttachmentSupport = -> [BaseFeature]
  Length = 20
  MapMode = 19
  Placement = pos=(285.756,986.528,40.945) rot=(0,0,1;0rad)
  ResizeMode = 0
FEATURE [PartDesign::Pad] Pad
  BaseFeature = -> BaseFeature
  Direction = (-9.79e-14,5.78e-13,-1)
  Length = 10
  Length2 = 10
  Profile = -> BaseFeature [Face82]
  Refine = true
  Suppressed = false
  Type = 3
  UpToFace = -> BaseFeature [Face23]
FEATURE [PartDesign::Pad] Pad001
  BaseFeature = -> Pad
  Direction = (5.33e-14,-4.564e-13,1)
  Length = 10
  Length2 = 10
  Profile = -> Pad [Edge192]
  Refine = true
  Suppressed = false
  Type = 3
  UpToFace = -> Pad [Face144]
FEATURE [Sketcher::SketchObject] Sketch
  ArcFitTolerance = 1e-06
  AttachmentSupport = -> [Pad001]
  ExternalGeometry = -> [DatumLine]
  FullyConstrained = true
  MakeInternals = false
  MapMode = 5
  Placement = pos=(2.0531e-12,-1.82128e-11,40.945) rot=(0,0,1;0rad)
  sketch-geometry (1):
    g0: Circle CenterX=285.756 CenterY=986.528 CenterZ=0 NormalX=0 NormalY=0 NormalZ=1 AngleXU=0 Radius=1.6
  constraints (2):
    c: Coincident(g0,g-3)
    c: Diameter(g0) = 3.2
FEATURE [PartDesign::Pocket] Pocket  label="rails_hole"
  BaseFeature = -> Pad001
  Direction = (-5.01e-14,4.448e-13,-1)
  Length = 10
  Length2 = 5
  Profile = -> Sketch
  ReferenceAxis = -> Sketch [N_Axis]
  Refine = true
  Suppressed = false
  Type = 0
FEATURE [PartDesign::Pocket] Pocket001  label="move_right_wall"
  BaseFeature = -> Pocket
  Direction = (1,-2.6e-15,1e-16)
  Length = 0.225
  Length2 = 5
  Profile = -> Pocket [Face11]
  Refine = true
  Suppressed = false
  Type = 0
FEATURE [PartDesign::Pad] Pad002  label="move_left_wall"
  BaseFeature = -> Pocket001
  Direction = (1,-2.6e-15,1e-16)
  Length = 0.215
  Length2 = 10
  Profile = -> Pocket001 [Face6]
  Refine = true
  Suppressed = false
  Type = 0
FEATURE [Sketcher::SketchObject] Sketch001
  ArcFitTolerance = 1e-06
  AttachmentSupport = -> [Pad002]
  ExternalGeometry = -> [DatumLine]
  FullyConstrained = true
  MakeInternals = false
  MapMode = 5
  Placement = pos=(-2.41256e-11,-5.0785e-12,32.8) rot=(1,0,0;3.14159rad)
  sketch-geometry (1):
    g0: Circle CenterX=285.756 CenterY=-986.528 CenterZ=0 NormalX=0 NormalY=0 NormalZ=1 AngleXU=0 Radius=1.95
  constraints (2):
    c: Coincident(g0,g-3)
    c: Diameter(g0) = 3.9
FEATURE [PartDesign::Pocket] Pocket002  label="rail_heat_insert"
  BaseFeature = -> Pad002
  Direction = (-7.355e-13,-1.548e-13,1)
  Length = 5.1
  Length2 = 5
  Profile = -> Sketch001
  ReferenceAxis = -> Sketch001 [N_Axis]
  Refine = true
  Suppressed = false
  Type = 0
FEATURE [PartDesign::Body] Body  label="k1_motor_mount_couplers_stock_right"
  AllowCompound = false
  BaseFeature = -> Part__Feature
  Group = -> [BaseFeature,DatumLine,Pad,Pad001,Sketch,Pocket,Pocket001,Pad002,Sketch001,Pocket002]
  Origin = -> Origin
  Placement = pos=(-200,-900,68) rot=(0,0,1;0rad)
  Tip = -> Pocket002
FEATURE [App::Part] Part  label="k1_motor_mount_couplers_stock_right_part"
  Group = -> [Part__Feature,Body,Link,Link001,Link002,Link003,Link004,Link005,Link006,Link007,Link008]
  Origin = -> Origin001
---- part k1_motor_mount_left.FCStd = doc fcstd_1f88776460f2 ----
FCSTD DOCUMENT  (FreeCAD 1.0R38641 +468 (Git))
Label: k1_motor_mount_left
License: All rights reserved
LicenseURL: https://en.wikipedia.org/wiki/All_rights_reserved
objects: App::Link×4, Part::Feature×1, PartDesign::FeatureBase×1, PartDesign::Body×1, App::Part×1
note: 4 computed .brp shape members not serialized (recipe doc carries the construction recipe); baked Part::Feature solids carry a one-line shape summary decoded from their .brp
EXTERNAL_REF file=cad_powge_pulley.FCStd obj=Part
EXTERNAL_REF file=cad_nema17_42_60.FCStd obj=COMPOUND049
EXTERNAL_REF file=cad_20T_15mm_pulley.FCStd obj=Part

FEATURE [Part::Feature] Part__Feature  label="step"
  shape: bbox 73.5 x 47.7 x 47.95 mm, 115 faces (baked)
FEATURE [PartDesign::FeatureBase] BaseFeature
  BaseFeature = -> Part__Feature
  Suppressed = false
FEATURE [PartDesign::Body] Body  label="k1_motor_mount_left"
  AllowCompound = false
  BaseFeature = -> Part__Feature
  Group = -> [BaseFeature]
  Origin = -> Origin
  Placement = pos=(-52,-950,0) rot=(0,0,1;0rad)
  Tip = -> BaseFeature
FEATURE [App::Link] Link  label="cad_powge_pulley_top_link"
  LinkPlacement = pos=(12.1406,50.0783,20.85) rot=(0,0,1;0rad)
  LinkedObject = -> <external cad_powge_pulley.FCStd>#Part
  Placement = pos=(12.1406,50.0783,20.85) rot=(0,0,1;0rad)
FEATURE [App::Link] Link001  label="cad_powge_pulley_bottom_link"
  LinkPlacement = pos=(12.1406,50.0783,9.7) rot=(0,0,1;0rad)
  LinkedObject = -> <external cad_powge_pulley.FCStd>#Part
  Placement = pos=(12.1406,50.0783,9.7) rot=(0,0,1;0rad)
FEATURE [App::Link] Link002  label="cad_nema17_link"
  LinkPlacement = pos=(27.6406,34.5783,-16.802) rot=(0,0,1;0rad)
  LinkedObject = -> <external cad_nema17_42_60.FCStd>#COMPOUND049
  Placement = pos=(27.6406,34.5783,-16.802) rot=(0,0,1;0rad)
FEATURE [App::Link] Link003  label="cad_20T_pulley"
  LinkPlacement = pos=(115.263,-34.4991,1.64211) rot=(0,1,0;3.14159rad)
  LinkedObject = -> <external cad_20T_15mm_pulley.FCStd>#Part
  Placement = pos=(115.263,-34.4991,1.64211) rot=(0,1,0;3.14159rad)
FEATURE [App::Part] Part  label="k1_motor_mount_left_part"
  Group = -> [Part__Feature,Body,Link,Link001,Link002,Link003]
  Origin = -> Origin001
---- part k1_motor_mount_right.FCStd = doc fcstd_ee01133c09cf ----
FCSTD DOCUMENT  (FreeCAD 1.0R38641 +468 (Git))
Label: k1_motor_mount_right
License: All rights reserved
LicenseURL: https://en.wikipedia.org/wiki/All_rights_reserved
objects: App::Link×4, Part::Feature×1, PartDesign::FeatureBase×1, PartDesign::Body×1, App::Part×1
note: 4 computed .brp shape members not serialized (recipe doc carries the construction recipe); baked Part::Feature solids carry a one-line shape summary decoded from their .brp
EXTERNAL_REF file=cad_powge_pulley.FCStd obj=Part
EXTERNAL_REF file=cad_20T_15mm_pulley.FCStd obj=Part
EXTERNAL_REF file=cad_nema17_42_60.FCStd obj=COMPOUND049

FEATURE [Part::Feature] Part__Feature  label="step"
  shape: bbox 73.5 x 47.7 x 47.95 mm, 120 faces (baked)
FEATURE [PartDesign::FeatureBase] BaseFeature
  BaseFeature = -> Part__Feature
  Suppressed = false
FEATURE [PartDesign::Body] Body  label="k1_motor_mount_right"
  AllowCompound = false
  BaseFeature = -> Part__Feature
  Group = -> [BaseFeature]
  Origin = -> Origin001
  Placement = pos=(-229,-950,0) rot=(0,0,1;0rad)
  Tip = -> BaseFeature
FEATURE [App::Link] Link  label="cad_powge_pulley_top_link"
  LinkPlacement = pos=(65.1406,50.0783,20.8) rot=(0,0,1;0rad)
  LinkedObject = -> <external cad_powge_pulley.FCStd>#Part
  Placement = pos=(65.1406,50.0783,20.8) rot=(0,0,1;0rad)
FEATURE [App::Link] Link001  label="cad_powge_pulley_bottom_link"
  LinkPlacement = pos=(65.1406,50.0783,9.7) rot=(0,0,1;0rad)
  LinkedObject = -> <external cad_powge_pulley.FCStd>#Part
  Placement = pos=(65.1406,50.0783,9.7) rot=(0,0,1;0rad)
FEATURE [App::Link] Link002  label="cad_20T_pulley_link"
  LinkPlacement = pos=(-37.9821,-34.499,38.8079) rot=(0,0,1;0rad)
  LinkedObject = -> <external cad_20T_15mm_pulley.FCStd>#Part
  Placement = pos=(-37.9821,-34.499,38.8079) rot=(0,0,1;0rad)
FEATURE [App::Link] Link003  label="cad_nema17_link"
  LinkPlacement = pos=(49.6406,34.5783,-16.702) rot=(0,0,1;3.14159rad)
  LinkedObject = -> <external cad_nema17_42_60.FCStd>#COMPOUND049
  Placement = pos=(49.6406,34.5783,-16.702) rot=(0,0,1;3.14159rad)
FEATURE [App::Part] Part  label="k1_motor_mount_right_part"
  Group = -> [Body,Link,Link001,Link002,Link003]
  Origin = -> Origin
---- part k1_rail_mount.FCStd = doc fcstd_008f81dd06c1 ----
FCSTD DOCUMENT  (FreeCAD 1.0R38641 +468 (Git))
Label: k1_rail_mount
License: All rights reserved
LicenseURL: https://en.wikipedia.org/wiki/All_rights_reserved
objects: Part::Feature×1, PartDesign::FeatureBase×1, Sketcher::SketchObject×1, PartDesign::Pocket×1, PartDesign::Body×1, App::Part×1
note: 9 computed .brp shape members not serialized (recipe doc carries the construction recipe); baked Part::Feature solids carry a one-line shape summary decoded from their .brp

FEATURE [Part::Feature] Part__Feature  label="step"
  shape: bbox 25 x 40 x 29 mm, 18 faces (baked)
FEATURE [PartDesign::FeatureBase] BaseFeature
  BaseFeature = -> Part__Feature
  Suppressed = false
FEATURE [Sketcher::SketchObject] Sketch
  ArcFitTolerance = 1e-06
  AttachmentSupport = -> [BaseFeature]
  ExternalGeometry = -> [BaseFeature]
  FullyConstrained = true
  MakeInternals = false
  MapMode = 5
  Placement = pos=(0,0,0) rot=(1,0,0;1.5708rad)
  sketch-geometry (3):
    g0: LineSegment StartX=25 StartY=1 StartZ=0 EndX=24.4938 EndY=30 EndZ=0
    g1: LineSegment StartX=24.4938 StartY=30 StartZ=0 EndX=25 EndY=30 EndZ=0
    g2: LineSegment StartX=25 StartY=30 StartZ=0 EndX=25 EndY=1 EndZ=0
  constraints (7):
    c: Coincident(g0,g-3)
    c: PointOnObject(g0,g-4)
    c: Coincident(g1,g0)
    c: Coincident(g1,g-4)
    c: Coincident(g2,g1)
    c: Coincident(g2,g0)
    c: Angle(g2,g0) = 0.0174533
FEATURE [PartDesign::Pocket] Pocket
  BaseFeature = -> BaseFeature
  Direction = (0,1,-2e-16)
  Length = 5
  Length2 = 5
  Profile = -> Sketch
  ReferenceAxis = -> Sketch [N_Axis]
  Refine = true
  Suppressed = false
  Type = 1
FEATURE [PartDesign::Body] Body  label="k1_rail_mount"
  AllowCompound = false
  BaseFeature = -> Part__Feature
  Group = -> [BaseFeature,Sketch,Pocket]
  Origin = -> Origin001
  Tip = -> Pocket
FEATURE [App::Part] Part  label="k1_rail_mount_part"
  Group = -> [Body]
  Origin = -> Origin
---- part k1_tensioner_left.FCStd = doc fcstd_c65c4d3c9184 ----
FCSTD DOCUMENT  (FreeCAD 1.0R38641 +468 (Git))
Label: k1_tensioner_left
License: All rights reserved
LicenseURL: https://en.wikipedia.org/wiki/All_rights_reserved
objects: Part::Feature×1, PartDesign::FeatureBase×1, PartDesign::Body×1, App::Link×1, App::Part×1
note: 4 computed .brp shape members not serialized (recipe doc carries the construction recipe); baked Part::Feature solids carry a one-line shape summary decoded from their .brp
EXTERNAL_REF file=cad_powge_pulley.FCStd obj=Part

FEATURE [Part::Feature] Part__Feature  label="step"
  shape: bbox 14.4 x 34.9 x 33 mm, 57 faces (baked)
FEATURE [PartDesign::FeatureBase] BaseFeature
  BaseFeature = -> Part__Feature
  Suppressed = false
FEATURE [PartDesign::Body] Body  label="k1_tensioner_left"
  AllowCompound = false
  BaseFeature = -> Part__Feature
  Group = -> [BaseFeature]
  Origin = -> Origin001
  Tip = -> BaseFeature
FEATURE [App::Link] Link  label="cad_powge_pulley_link"
  LinkPlacement = pos=(5.2,-18.65,6.7) rot=(-1,0,0;1.5708rad)
  LinkedObject = -> <external cad_powge_pulley.FCStd>#Part
  Placement = pos=(5.2,-18.65,6.7) rot=(-1,0,0;1.5708rad)
FEATURE [App::Part] Part  label="k1_tensioner_left_part"
  Group = -> [Body,Link]
  Origin = -> Origin
  Placement = pos=(0,0,0) rot=(0.57735,0.57735,0.57735;2.0944rad)
---- part k1_tensioner_right.FCStd = doc fcstd_b45f1fe96978 ----
FCSTD DOCUMENT  (FreeCAD 1.0R38641 +468 (Git))
Label: k1_tensioner_right
License: All rights reserved
LicenseURL: https://en.wikipedia.org/wiki/All_rights_reserved
objects: Part::Feature×1, App::Link×1, PartDesign::FeatureBase×1, PartDesign::Body×1, App::Part×1
note: 4 computed .brp shape members not serialized (recipe doc carries the construction recipe); baked Part::Feature solids carry a one-line shape summary decoded from their .brp
EXTERNAL_REF file=cad_powge_pulley.FCStd obj=Part

FEATURE [Part::Feature] Part__Feature  label="step"
  shape: bbox 14.6 x 34.9 x 33 mm, 55 faces (baked)
FEATURE [App::Link] Link  label="cad_powge_pulley_link"
  LinkPlacement = pos=(5.3,-27.85,6.7) rot=(-1,0,0;1.5708rad)
  LinkedObject = -> <external cad_powge_pulley.FCStd>#Part
  Placement = pos=(5.3,-27.85,6.7) rot=(-1,0,0;1.5708rad)
FEATURE [PartDesign::FeatureBase] BaseFeature
  BaseFeature = -> Part__Feature
  Suppressed = false
FEATURE [PartDesign::Body] Body  label="k1_tensioner_right"
  AllowCompound = false
  BaseFeature = -> Part__Feature
  Group = -> [BaseFeature]
  Origin = -> Origin001
  Tip = -> BaseFeature
FEATURE [App::Part] Part  label="k1_tensioner_right_part"
  Group = -> [Body,Link]
  Origin = -> Origin
  Placement = pos=(0,0,0) rot=(0.57735,-0.57735,-0.57735;2.0944rad)
---- part k1_toolhead_20x10.FCStd = doc fcstd_8714f6a44a14 ----
FCSTD DOCUMENT  (FreeCAD 1.0R38641 +468 (Git))
Label: k1_toolhead_20x10
License: All rights reserved
LicenseURL: https://en.wikipedia.org/wiki/All_rights_reserved
objects: App::Link×3, Part::Feature×1, PartDesign::FeatureBase×1, PartDesign::Body×1, App::Part×1
note: 4 computed .brp shape members not serialized (recipe doc carries the construction recipe); baked Part::Feature solids carry a one-line shape summary decoded from their .brp
EXTERNAL_REF file=cad_mgn12h_block.FCStd obj=Body
EXTERNAL_REF file=cad_hotend.FCStd obj=K1_Hotend
EXTERNAL_REF file=cad_extruder.FCStd obj=K1_extruder

FEATURE [Part::Feature] Part__Feature  label="step"
  shape: bbox 64.04 x 48.4 x 74 mm, 251 faces (baked)
FEATURE [PartDesign::FeatureBase] BaseFeature
  BaseFeature = -> Part__Feature
  Suppressed = false
FEATURE [PartDesign::Body] Body  label="k1_toolhead_20x10"
  AllowCompound = false
  BaseFeature = -> Part__Feature
  Group = -> [BaseFeature]
  Origin = -> Origin001
  Tip = -> BaseFeature
FEATURE [App::Link] Link  label="cad_mgn12_link"
  LinkPlacement = pos=(-0.49,-22.7,31.1) rot=(0.707107,0.707107,0;3.14159rad)
  LinkedObject = -> <external cad_mgn12h_block.FCStd>#Body
  Placement = pos=(-0.49,-22.7,31.1) rot=(0.707107,0.707107,0;3.14159rad)
FEATURE [App::Link] Link001  label="cad_hotend_link"
  LinkedObject = -> <external cad_hotend.FCStd>#K1_Hotend
FEATURE [App::Link] Link002  label="cad_extruder_link"
  LinkPlacement = pos=(2.30001,-0.299999,53.5) rot=(0,0,1;1.5708rad)
  LinkedObject = -> <external cad_extruder.FCStd>#K1_extruder
  Placement = pos=(2.30001,-0.299999,53.5) rot=(0,0,1;1.5708rad)
FEATURE [App::Part] Part  label="k1_toolhead_20x10_part"
  Group = -> [Body,Link,Link001,Link002]
  Origin = -> Origin
